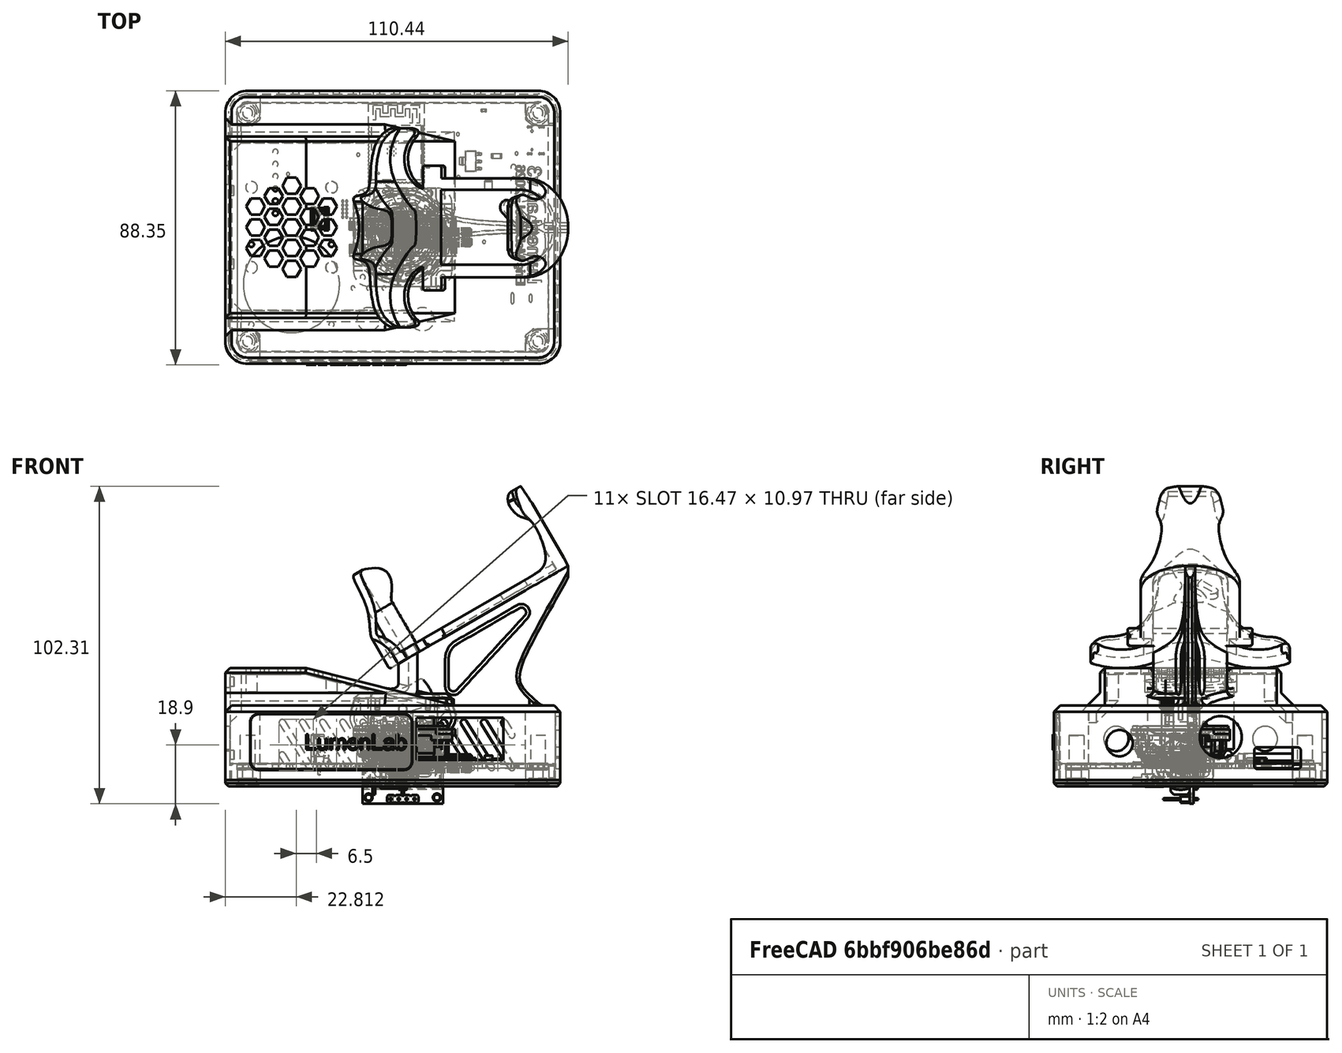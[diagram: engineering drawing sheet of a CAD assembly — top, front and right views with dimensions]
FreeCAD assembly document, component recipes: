
FREECAD ASSEMBLY — COMPONENT RECIPES ("lumenlab-platform-enclosure")

This assembly document has 22 components, labeled P0..P21 below (a component is one placed body or linked part). 21 of them carry a construction recipe — the FreeCAD feature program that regenerates the part from scratch, quoted from this document or its linked companion documents; the rest are supplied as boundary geometry only. No exploded tour is included for this assembly.
NOTE — this tour is split across 2 documents so each fits a 32k-token context. This is document 1: the component sections continue in the remaining 1 document, each repeating the header above.
COMPONENT P0 — geometry summary ("lumenlab-pcb001"; no construction recipe available for this part):
  bounding box: 106.5 x 80.0 x 42.6 mm
  tessellated surface: 375,475 triangles
  volume: 30416 mm^3 (8% of its bounding box)
COMPONENT P1 — recipe-attached ("lid", modeled in this document).
Construction recipe (the document's own serialized feature program — sketch geometry with constraints, then the solid features built on it; lengths are millimeters unless a unit is written):

FEATURE [PartDesign::SubShapeBinder] Binder
  BindCopyOnChange = 0
  BindMode = 0
  ClaimChildren = false
  Context = -> Body [Binder.]
  Fuse = false
  MakeFace = true
  OffsetFill = false
  OffsetIntersection = false
  OffsetJoinType = 0
  OffsetOpenResult = false
  PartialLoad = false
  Refine = true
  Relative = true
  Support = -> [Board_aaa008]
  _Version = 2
FEATURE [Sketcher::SketchObject] Sketch
  ArcFitTolerance = 1e-06
  AttachmentOffset = pos=(0,0,3.75) rot=(0,0,1;0rad)
  AttachmentSupport = -> [Binder]
  ExternalGeometry = -> [Binder]
  ExternalTypes = [0]
  FullyConstrained = true
  MakeInternals = false
  MapMode = 5
  Placement = pos=(0,0,-5.3502) rot=(1,0,0;3.14159rad)
  _ExternalGeoVersion = 0
  sketch-geometry (10):
    g0: LineSegment StartX=-57.1492 StartY=33.5464 StartZ=0 EndX=-57.1492 EndY=-39.9989 EndZ=0
    g1: LineSegment StartX=-49.9485 StartY=-47.1996 StartZ=0 EndX=43.5501 EndY=-47.1996 EndZ=0
    g2: LineSegment StartX=50.7508 StartY=-39.9989 StartZ=0 EndX=50.7508 EndY=33.5464 EndZ=0
    g3: LineSegment StartX=43.5501 StartY=40.7472 StartZ=0 EndX=-49.9485 EndY=40.7472 EndZ=0
    g4: ArcOfCircle CenterX=-49.9485 CenterY=33.5464 CenterZ=0 NormalX=0 NormalY=0 NormalZ=1 AngleXU=0 Radius=7.20071 StartAngle=1.5708 EndAngle=3.14159
    g5: ArcOfCircle CenterX=-49.9485 CenterY=-39.9989 CenterZ=0 NormalX=0 NormalY=0 NormalZ=1 AngleXU=0 Radius=7.20071 StartAngle=3.14159 EndAngle=4.71239
    g6: ArcOfCircle CenterX=43.5501 CenterY=-39.9989 CenterZ=0 NormalX=0 NormalY=0 NormalZ=1 AngleXU=0 Radius=7.20071 StartAngle=4.71239 EndAngle=6.28319
    g7: ArcOfCircle CenterX=43.5501 CenterY=33.5464 CenterZ=0 NormalX=0 NormalY=0 NormalZ=1 AngleXU=0 Radius=7.20071 StartAngle=1e-16 EndAngle=1.5708
    g8: GeomPoint [constr] X=-57.1492 Y=40.7472 Z=0
    g9: GeomPoint [constr] X=50.7508 Y=-47.1996 Z=0
  constraints (23):
    c: Tangent(g0,g4) = -1.5708
    c: Tangent(g0,g5) = -1.5708
    c: Tangent(g1,g5) = -1.5708
    c: Tangent(g1,g6) = -1.5708
    c: Tangent(g2,g6) = -1.5708
    c: Tangent(g2,g7) = -1.5708
    c: Tangent(g3,g7) = -1.5708
    c: Tangent(g3,g4) = -1.5708
    c: Vertical(g0)
    c: Vertical(g2)
    c: Horizontal(g1)
    c: Horizontal(g3)
    c: Equal(g4,g5)
    c: Equal(g5,g6)
    c: Equal(g6,g7)
    c: PointOnObject(g8,g0)
    c: PointOnObject(g8,g3)
    c: PointOnObject(g9,g1)
    c: PointOnObject(g9,g2)
    c: DistanceX(g0,g-5) = 4  'enclosure-width'
    c: Coincident(g4,g-4)
    c: Distance(g-7,g2) = 4
    c: Distance(g-9,g1) = 4
FEATURE [PartDesign::Pad] Pad
  Direction = (0,0,-1)
  Length = 2
  Length2 = 10
  Profile = -> Sketch
  ReferenceAxis = -> Sketch [N_Axis]
  Refine = true
  SideType = 0
  Suppressed = false
  Type = 0
  Type2 = 0
FEATURE [Sketcher::SketchObject] Sketch001
  ArcFitTolerance = 1e-06
  AttachmentSupport = -> [Pad]
  ExternalGeometry = -> [Binder]
  ExternalTypes = [0]
  FullyConstrained = true
  MakeInternals = false
  MapMode = 5
  Placement = pos=(0,0,-5.3502) rot=(0,0,1;0rad)
  _ExternalGeoVersion = 0
  sketch-geometry (20):
    g0: LineSegment StartX=-55.15 StartY=39.9996 StartZ=0 EndX=-55.15 EndY=-33.5498 EndZ=0
    g1: LineSegment StartX=-49.95 StartY=-38.7498 StartZ=0 EndX=43.551 EndY=-38.7498 EndZ=0
    g2: LineSegment StartX=48.751 StartY=-33.5498 StartZ=0 EndX=48.751 EndY=39.9996 EndZ=0
    g3: LineSegment StartX=43.551 StartY=45.1996 StartZ=0 EndX=-49.95 EndY=45.1996 EndZ=0
    g4: ArcOfCircle CenterX=-49.95 CenterY=39.9996 CenterZ=0 NormalX=0 NormalY=0 NormalZ=1 AngleXU=0 Radius=5.19999 StartAngle=1.5708 EndAngle=3.14159
    g5: ArcOfCircle CenterX=-49.95 CenterY=-33.5498 CenterZ=0 NormalX=0 NormalY=0 NormalZ=1 AngleXU=0 Radius=5.19999 StartAngle=3.14159 EndAngle=4.71239
    g6: ArcOfCircle CenterX=43.551 CenterY=-33.5498 CenterZ=0 NormalX=0 NormalY=0 NormalZ=1 AngleXU=0 Radius=5.19999 StartAngle=4.71239 EndAngle=6.28319
    g7: ArcOfCircle CenterX=43.551 CenterY=39.9996 CenterZ=0 NormalX=0 NormalY=0 NormalZ=1 AngleXU=0 Radius=5.19999 StartAngle=5e-16 EndAngle=1.5708
    g8: GeomPoint [constr] X=-55.15 Y=45.1996 Z=0
    g9: GeomPoint [constr] X=48.751 Y=-38.7498 Z=0
    g10: LineSegment StartX=-53.35 StartY=39.9996 StartZ=0 EndX=-53.35 EndY=-33.5498 EndZ=0
    g11: LineSegment StartX=-49.95 StartY=-36.9498 StartZ=0 EndX=43.551 EndY=-36.9498 EndZ=0
    g12: LineSegment StartX=46.951 StartY=-33.5498 StartZ=0 EndX=46.951 EndY=39.9996 EndZ=0
    g13: LineSegment StartX=43.551 StartY=43.3996 StartZ=0 EndX=-49.95 EndY=43.3996 EndZ=0
    g14: ArcOfCircle CenterX=-49.95 CenterY=39.9996 CenterZ=0 NormalX=0 NormalY=0 NormalZ=1 AngleXU=0 Radius=3.39999 StartAngle=1.5708 EndAngle=3.14159
    g15: ArcOfCircle CenterX=-49.95 CenterY=-33.5498 CenterZ=0 NormalX=0 NormalY=0 NormalZ=1 AngleXU=0 Radius=3.39999 StartAngle=3.14159 EndAngle=4.71239
    g16: ArcOfCircle CenterX=43.551 CenterY=-33.5498 CenterZ=0 NormalX=0 NormalY=0 NormalZ=1 AngleXU=0 Radius=3.39999 StartAngle=4.71239 EndAngle=6.28319
    g17: ArcOfCircle CenterX=43.551 CenterY=39.9996 CenterZ=0 NormalX=0 NormalY=0 NormalZ=1 AngleXU=0 Radius=3.39999 StartAngle=0 EndAngle=1.5708
    g18: GeomPoint [constr] X=-53.35 Y=43.3996 Z=0
    g19: GeomPoint [constr] X=46.951 Y=-36.9498 Z=0
  constraints (46):
    c: Tangent(g0,g4) = -1.5708
    c: Tangent(g0,g5) = -1.5708
    c: Tangent(g1,g5) = -1.5708
    c: Tangent(g1,g6) = -1.5708
    c: Tangent(g2,g6) = -1.5708
    c: Tangent(g2,g7) = -1.5708
    c: Tangent(g3,g7) = -1.5708
    c: Tangent(g3,g4) = -1.5708
    c: Vertical(g0)
    c: Vertical(g2)
    c: Horizontal(g1)
    c: Horizontal(g3)
    c: Equal(g4,g5)
    c: Equal(g5,g6)
    c: Equal(g6,g7)
    c: PointOnObject(g8,g0)
    c: PointOnObject(g8,g3)
    c: PointOnObject(g9,g1)
    c: PointOnObject(g9,g2)
    c: DistanceX(g0,g-5) = 2
    c: Coincident(g4,g-4)
    c: DistanceX(g-7,g2) = 2
    c: DistanceY(g1,g-9) = 2
    c: Tangent(g10,g14) = -1.5708
    c: Tangent(g10,g15) = -1.5708
    c: Tangent(g11,g15) = -1.5708
    c: Tangent(g11,g16) = -1.5708
    c: Tangent(g12,g16) = -1.5708
    c: Tangent(g12,g17) = -1.5708
    c: Tangent(g13,g17) = -1.5708
    c: Tangent(g13,g14) = -1.5708
    c: Vertical(g10)
    c: Vertical(g12)
    c: Horizontal(g11)
    c: Horizontal(g13)
    c: Equal(g14,g15)
    c: Equal(g15,g16)
    c: Equal(g16,g17)
    c: PointOnObject(g18,g10)
    c: PointOnObject(g18,g13)
    c: PointOnObject(g19,g11)
    c: PointOnObject(g19,g12)
    c: DistanceX(g10,g-5) = 0.2
    c: DistanceX(g-7,g12) = 0.2
    c: DistanceY(g11,g-9) = 0.2
    c: Coincident(g14,g4)
FEATURE [PartDesign::Pad] Pad001
  BaseFeature = -> Pad
  Direction = (0,0,1)
  Length = 5
  Length2 = 10
  Profile = -> Sketch001
  ReferenceAxis = -> Sketch001 [N_Axis]
  Refine = true
  SideType = 0
  Suppressed = false
  Type = 0
  Type2 = 0
FEATURE [Sketcher::SketchObject] Sketch002
  ArcFitTolerance = 1e-06
  ExternalGeometry = -> [Binder,Pad001]
  ExternalTypes = [0]
  FullyConstrained = true
  MakeInternals = false
  MapMode = 5
  Placement = pos=(0,0,-2) rot=(1,0,0;3.14159rad)
  _ExternalGeoVersion = 0
  sketch-geometry (10):
    g0: LineSegment StartX=-53.1492 StartY=29.5498 StartZ=0 EndX=-53.35 EndY=29.5498 EndZ=0
    g1: LineSegment StartX=-45.95 StartY=36.7473 StartZ=0 EndX=-45.95 EndY=36.9498 EndZ=0
    g2: LineSegment StartX=-45.95 StartY=36.9498 StartZ=0 EndX=-49.95 EndY=36.9498 EndZ=0
    g3: LineSegment StartX=-53.35 StartY=29.5498 StartZ=0 EndX=-53.35 EndY=33.5498 EndZ=0
    g4: ArcOfCircle CenterX=-49.95 CenterY=33.5498 CenterZ=0 NormalX=0 NormalY=0 NormalZ=1 AngleXU=0 Radius=3.39999 StartAngle=1.5708 EndAngle=3.14159
    g5: LineSegment StartX=-53.1492 StartY=29.5498 StartZ=0 EndX=-48.6466 EndY=29.5498 EndZ=0
    g6: ArcOfCircle CenterX=-48.6466 CenterY=30.4451 CenterZ=0 NormalX=0 NormalY=0 NormalZ=1 AngleXU=0 Radius=0.895293 StartAngle=4.71239 EndAngle=5.38086
    g7: LineSegment StartX=-48.0918 StartY=29.7425 StartZ=0 EndX=-46.138 EndY=31.2855 EndZ=0
    g8: ArcOfCircle CenterX=-46.4444 CenterY=31.6735 CenterZ=0 NormalX=0 NormalY=0 NormalZ=1 AngleXU=0 Radius=0.494368 StartAngle=5.38086 EndAngle=6.28319
    g9: LineSegment StartX=-45.95 StartY=31.6735 StartZ=0 EndX=-45.95 EndY=36.7473 EndZ=0
  constraints (24):
    c: PointOnObject(g0,g-8)
    c: Horizontal(g0)
    c: PointOnObject(g1,g-7)
    c: Vertical(g1)
    c: Coincident(g2,g1)
    c: Coincident(g2,g-9)
    c: Coincident(g3,g0)
    c: Coincident(g3,g-9)
    c: Coincident(g4,g2)
    c: Coincident(g4,g3)
    c: PointOnObject(g0,g-10)
    c: PointOnObject(g1,g-11)
    c: DistanceY(g3,g3) = 4
    c: DistanceX(g2,g2) = 4
    c: Equal(g4,g-9)
    c: Coincident(g0,g5)
    c: Tangent(g5,g6) = -1.5708
    c: Tangent(g6,g7) = -1.5708
    c: Tangent(g7,g8) = -1.5708
    c: Tangent(g8,g9) = -1.5708
    c: Vertical(g9)
    c: Coincident(g9,g1)
    c: Horizontal(g5)
    c: Block(g7)
FEATURE [PartDesign::Pad] Pad002
  BaseFeature = -> Pad001
  Direction = (0,-1e-16,-1)
  Length = 10
  Length2 = 10
  Profile = -> Sketch002
  ReferenceAxis = -> Sketch002 [N_Axis]
  Refine = true
  SideType = 0
  Suppressed = false
  Type = 2
  Type2 = 0
FEATURE [PartDesign::Plane] DatumPlane
  AttachmentOffset = pos=(0,0,0) rot=(1,0,0;1.5708rad)
  AttachmentSupport = -> [Pad002]
  Length = 122.59
  MapMode = 45
  Placement = pos=(-3.1995,3.22491,-2.8502) rot=(1,0,0;1.5708rad)
  ResizeMode = 0
  Width = 64.6901
  expr: .AttachmentOffset.Rotation.Pitch = 0
FEATURE [PartDesign::Plane] DatumPlane001
  AttachmentOffset = pos=(0,0,0) rot=(1,0,0;1.5708rad)
  AttachmentSupport = -> [Pad002]
  Length = 101.209
  MapMode = 45
  Placement = pos=(-3.1995,3.22491,-2.8502) rot=(0.57735,0.57735,0.57735;2.0944rad)
  ResizeMode = 0
  Width = 63.2625
FEATURE [PartDesign::Line] DatumLine
  AttacherType = Attacher::AttachEngineLine
  AttachmentSupport = -> [DatumPlane001,DatumPlane]
  Length = 20
  MapMode = 30
  Placement = pos=(-3.1995,3.22491,-2.8502) rot=(0,1,0;3.14159rad)
  ResizeMode = 0
FEATURE [PartDesign::Mirrored] Mirrored
  BaseFeature = -> Pad002
  MirrorPlane = -> DatumPlane
  Originals = -> [Pad002]
  Refine = true
  Suppressed = false
  TransformMode = 0
FEATURE [PartDesign::Mirrored] Mirrored001
  BaseFeature = -> Mirrored
  MirrorPlane = -> DatumPlane001
  Originals = -> [Pad002]
  Refine = true
  Suppressed = false
  TransformMode = 0
FEATURE [PartDesign::PolarPattern] PolarPattern
  Angle = 360
  Axis = -> DatumLine
  BaseFeature = -> Mirrored001
  Mode = 0
  Occurrences = 2
  Offset = 120
  Originals = -> [Pad002]
  Refine = true
  Reversed = true
  SpacingPattern = [0]
  Spacings = [-1]
  Suppressed = false
  TransformMode = 0
FEATURE [Sketcher::SketchObject] Sketch003
  ArcFitTolerance = 1e-06
  AttachmentSupport = -> [PolarPattern]
  ExternalTypes = [0]
  FullyConstrained = true
  MakeInternals = false
  MapMode = 5
  Placement = pos=(0,0,-2) rot=(0,0,1;0rad)
  _ExternalGeoVersion = 0
  sketch-geometry (1):
    g0: Circle CenterX=-49.95 CenterY=-33.5498 CenterZ=0 NormalX=0 NormalY=0 NormalZ=1 AngleXU=0 Radius=1.625
  constraints (2):
    c: Coincident(g0,g-3)
    c: Diameter(g0) = 3.25
FEATURE [PartDesign::Pocket] Pocket
  BaseFeature = -> PolarPattern
  Direction = (0,0,-1)
  Length = 4.35
  Length2 = 5
  Profile = -> Sketch003
  ReferenceAxis = -> Sketch003 [N_Axis]
  Refine = true
  SideType = 0
  Suppressed = false
  Type = 1
  Type2 = 0
FEATURE [PartDesign::Mirrored] Mirrored002
  BaseFeature = -> Pocket
  MirrorPlane = -> DatumPlane
  Originals = -> [Pocket]
  Refine = true
  Suppressed = false
  TransformMode = 0
FEATURE [PartDesign::Mirrored] Mirrored003
  BaseFeature = -> Mirrored002
  MirrorPlane = -> DatumPlane001
  Originals = -> [Pocket]
  Refine = true
  Suppressed = false
  TransformMode = 0
FEATURE [PartDesign::PolarPattern] PolarPattern001
  Angle = 360
  Axis = -> DatumLine
  BaseFeature = -> Mirrored003
  Mode = 0
  Occurrences = 2
  Offset = 120
  Originals = -> [Pocket]
  Refine = true
  SpacingPattern = [0]
  Spacings = [-1]
  Suppressed = false
  TransformMode = 0
FEATURE [Sketcher::SketchObject] Sketch046
  ArcFitTolerance = 1e-06
  AttachmentSupport = -> [PolarPattern001]
  ExternalGeometry = -> [PolarPattern001]
  ExternalTypes = [0,0,0,0]
  FullyConstrained = true
  MakeInternals = false
  MapMode = 5
  Placement = pos=(0,0,-7.3502) rot=(1,0,0;3.14159rad)
  _ExternalGeoVersion = 1
  sketch-geometry (4):
    g0: Circle CenterX=-49.95 CenterY=33.5498 CenterZ=0 NormalX=0 NormalY=0 NormalZ=1 AngleXU=0 Radius=3
    g1: Circle CenterX=43.551 CenterY=33.5498 CenterZ=0 NormalX=0 NormalY=0 NormalZ=1 AngleXU=0 Radius=3
    g2: Circle CenterX=43.551 CenterY=-39.9996 CenterZ=0 NormalX=0 NormalY=0 NormalZ=1 AngleXU=0 Radius=3
    g3: Circle CenterX=-49.95 CenterY=-39.9996 CenterZ=0 NormalX=0 NormalY=0 NormalZ=1 AngleXU=0 Radius=3
  constraints (8):
    c: Coincident(g0,g-6)
    c: Coincident(g1,g-5)
    c: Coincident(g2,g-4)
    c: Coincident(g3,g-3)
    c: Diameter(g0) = 6
    c: Equal(g0,g1)
    c: Equal(g0,g3)
    c: Equal(g0,g2)
FEATURE [PartDesign::Pocket] Pocket023
  BaseFeature = -> PolarPattern001
  Direction = (0,0,1)
  Length = 2.5
  Length2 = 5
  Profile = -> Sketch046
  ReferenceAxis = -> Sketch046 [N_Axis]
  Refine = true
  SideType = 0
  Suppressed = false
  Type = 0
  Type2 = 0
FEATURE [Sketcher::SketchObject] Sketch067
  ArcFitTolerance = 1e-06
  AttachmentSupport = -> [Pocket023]
  ExternalGeometry = -> [Pocket023]
  ExternalTypes = [0,0,0,0]
  FullyConstrained = true
  MakeInternals = false
  MapMode = 5
  Placement = pos=(0,0,-7.3502) rot=(1,0,0;3.14159rad)
  _ExternalGeoVersion = 1
  sketch-geometry (4):
    g0: Circle CenterX=-49.95 CenterY=33.5498 CenterZ=0 NormalX=0 NormalY=0 NormalZ=1 AngleXU=0 Radius=3.625
    g1: Circle CenterX=43.551 CenterY=33.5498 CenterZ=0 NormalX=0 NormalY=0 NormalZ=1 AngleXU=0 Radius=3.625
    g2: Circle CenterX=43.551 CenterY=-39.9996 CenterZ=0 NormalX=0 NormalY=0 NormalZ=1 AngleXU=0 Radius=3.625
    g3: Circle CenterX=-49.95 CenterY=-39.9996 CenterZ=0 NormalX=0 NormalY=0 NormalZ=1 AngleXU=0 Radius=3.625
  constraints (8):
    c: Diameter(g0) = 7.25
    c: Coincident(g0,g-3)
    c: Coincident(g1,g-4)
    c: Coincident(g2,g-5)
    c: Coincident(g3,g-6)
    c: Equal(g0,g1)
    c: Equal(g0,g3)
    c: Equal(g0,g2)
FEATURE [PartDesign::Pocket] Pocket033
  BaseFeature = -> Pocket023
  Direction = (0,0,1)
  Length = 0.5
  Length2 = 5
  Profile = -> Sketch067
  ReferenceAxis = -> Sketch067 [N_Axis]
  Refine = true
  SideType = 0
  Suppressed = false
  Type = 0
  Type2 = 0
FEATURE [Part::Part2DObjectPython] ShapeString002  # Draft 2D object (typed FeaturePython)
  FontFile = <path>
  Fuse = false
  Justification = 6
  JustificationReference = 0
  KeepLeftMargin = false
  MakeFace = true
  ObliqueAngle = 0
  Placement = pos=(40.1807,-14.5677,-7.3502) rot=(0.707107,0.707107,0;3.14159rad)
  ScaleToSize = true
  Size = 4.5
  String = LumenLab v3
  Tracking = 0
FEATURE [Part::Part2DObjectPython] ShapeString003  # Draft 2D object (typed FeaturePython)
  FontFile = <path>
  Fuse = false
  Justification = 6
  JustificationReference = 0
  KeepLeftMargin = false
  MakeFace = true
  ObliqueAngle = 0
  Placement = pos=(36.4305,-15.2766,-7.3502) rot=(0.707107,0.707107,0;3.14159rad)
  ScaleToSize = true
  Size = 3
  String = Eric McDaniel - 2026
  Tracking = 0
FEATURE [PartDesign::Chamfer] Chamfer014
  Angle = 45
  Base = -> Pocket033 [Edge24]
  BaseFeature = -> Pocket033
  ChamferType = 0
  FlipDirection = false
  Refine = true
  Size = 1
  Size2 = 1
  SupportTransform = false
  Suppressed = false
  UseAllEdges = false
FEATURE [PartDesign::Pocket] Pocket034
  BaseFeature = -> Chamfer014
  Direction = (0,0,1)
  Length = 0.5
  Length2 = 5
  Profile = -> ShapeString002
  ReferenceAxis = -> ShapeString002 [N_Axis]
  Refine = true
  SideType = 0
  Suppressed = false
  Type = 0
  Type2 = 0
FEATURE [PartDesign::Pocket] Pocket035
  BaseFeature = -> Pocket034
  Direction = (0,0,1)
  Length = 0.5
  Length2 = 5
  Profile = -> ShapeString003
  ReferenceAxis = -> ShapeString003 [N_Axis]
  Refine = true
  SideType = 0
  Suppressed = false
  Type = 0
  Type2 = 0
FEATURE [Sketcher::SketchObject] Sketch070
  ArcFitTolerance = 1e-06
  AttachmentSupport = -> [Pocket035]
  ExternalGeometry = -> [Pocket035]
  ExternalTypes = [0,0,0,0]
  FullyConstrained = true
  MakeInternals = false
  MapMode = 5
  Placement = pos=(48.751,0,0) rot=(0.57735,0.57735,0.57735;2.0944rad)
  _ExternalGeoVersion = 1
  sketch-geometry (4):
    g0: LineSegment StartX=35.9996 StartY=-5.3502 StartZ=0 EndX=35.9996 EndY=-0.350198 EndZ=0
    g1: LineSegment StartX=35.9996 StartY=-0.350198 StartZ=0 EndX=2.99961 EndY=-0.350198 EndZ=0
    g2: LineSegment StartX=2.99961 StartY=-0.350198 StartZ=0 EndX=2.99961 EndY=-5.3502 EndZ=0
    g3: LineSegment StartX=2.99961 StartY=-5.3502 StartZ=0 EndX=35.9996 EndY=-5.3502 EndZ=0
  constraints (12):
    c: Coincident(g0,g1)
    c: Coincident(g2,g3)
    c: Coincident(g3,g0)
    c: Vertical(g0)
    c: Vertical(g2)
    c: Horizontal(g1)
    c: Horizontal(g3)
    c: PointOnObject(g0,g-4)
    c: PointOnObject(g-3,g0)
    c: Coincident(g2,g1)
    c: PointOnObject(g1,g-5)
    c: DistanceX(g1,g1) = 33
FEATURE [PartDesign::Pocket] Pocket037
  BaseFeature = -> Pocket035
  Direction = (-1,0,0)
  Length = 5
  Length2 = 5
  Profile = -> Sketch070
  ReferenceAxis = -> Sketch070 [N_Axis]
  Refine = true
  SideType = 0
  Suppressed = false
  Type = 2
  Type2 = 0
FEATURE [PartDesign::Chamfer] Chamfer015
  Angle = 45
  Base = -> Pocket037 [Edge1565,Edge1564,Edge1554]
  BaseFeature = -> Pocket037
  ChamferType = 0
  FlipDirection = false
  Refine = true
  Size = 0.6
  Size2 = 1
  SupportTransform = false
  Suppressed = false
  UseAllEdges = false
FEATURE [PartDesign::Body] Body  label="lid"
  AllowCompound = false
  Group = -> [Binder,Sketch,Pad,Sketch001,Pad001,Sketch002,Pad002,DatumPlane,Mirrored,DatumPlane001,Mirrored001,DatumLine,PolarPattern,Sketch003,Pocket,Mirrored002,Mirrored003,PolarPattern001,Sketch046,Pocket023,Sketch067,Pocket033,Chamfer014,ShapeString002,ShapeString003,Pocket034,Pocket035,Sketch070,Pocket037,Chamfer015]
  Origin = -> Origin032
  Tip = -> Chamfer015
COMPONENT P2 — recipe-attached ("body", modeled in this document).
Construction recipe (the document's own serialized feature program — sketch geometry with constraints, then the solid features built on it; lengths are millimeters unless a unit is written):

FEATURE [PartDesign::SubShapeBinder] Binder001
  BindCopyOnChange = 0
  BindMode = 0
  ClaimChildren = false
  Context = -> Body001 [Binder001.]
  Fuse = false
  MakeFace = true
  OffsetFill = false
  OffsetIntersection = false
  OffsetJoinType = 0
  OffsetOpenResult = false
  PartialLoad = false
  Refine = true
  Relative = true
  Support = -> [Board_aaa008]
  _Version = 2
FEATURE [Sketcher::SketchObject] Sketch010
  ArcFitTolerance = 1e-06
  AttachmentOffset = pos=(0,0,3.75) rot=(0,0,1;0rad)
  AttachmentSupport = -> [Binder001]
  ExternalGeometry = -> [Binder001]
  ExternalTypes = [0]
  FullyConstrained = true
  MakeInternals = false
  MapMode = 5
  Placement = pos=(0,0,-5.3502) rot=(1,0,0;3.14159rad)
  _ExternalGeoVersion = 0
  sketch-geometry (19):
    g0: LineSegment StartX=-57.1492 StartY=33.5464 StartZ=0 EndX=-57.1492 EndY=-39.9996 EndZ=0
    g1: LineSegment StartX=-49.9492 StartY=-47.1996 StartZ=0 EndX=43.5508 EndY=-47.1996 EndZ=0
    g2: LineSegment StartX=50.7508 StartY=-39.9996 StartZ=0 EndX=50.7508 EndY=33.5464 EndZ=0
    g3: LineSegment StartX=43.5508 StartY=40.7464 StartZ=0 EndX=-49.9492 EndY=40.7464 EndZ=0
    g4: ArcOfCircle CenterX=-49.9492 CenterY=33.5464 CenterZ=0 NormalX=0 NormalY=0 NormalZ=1 AngleXU=0 Radius=7.19996 StartAngle=1.5708 EndAngle=3.14159
    g5: ArcOfCircle CenterX=-49.9492 CenterY=-39.9996 CenterZ=0 NormalX=0 NormalY=0 NormalZ=1 AngleXU=0 Radius=7.19996 StartAngle=3.14159 EndAngle=4.71239
    g6: ArcOfCircle CenterX=43.5508 CenterY=-39.9996 CenterZ=0 NormalX=0 NormalY=0 NormalZ=1 AngleXU=0 Radius=7.19996 StartAngle=4.71239 EndAngle=6.28319
    g7: ArcOfCircle CenterX=43.5508 CenterY=33.5464 CenterZ=0 NormalX=0 NormalY=0 NormalZ=1 AngleXU=0 Radius=7.19996 StartAngle=0 EndAngle=1.5708
    g8: GeomPoint [constr] X=-57.1492 Y=40.7464 Z=0
    g9: GeomPoint [constr] X=50.7508 Y=-47.1996 Z=0
    g10: LineSegment StartX=-49.9492 StartY=-45.5996 StartZ=0 EndX=43.5508 EndY=-45.5996 EndZ=0
    g11: LineSegment StartX=49.1508 StartY=-39.9996 StartZ=0 EndX=49.1508 EndY=33.5464 EndZ=0
    g12: LineSegment StartX=43.5508 StartY=39.1464 StartZ=0 EndX=-49.9492 EndY=39.1464 EndZ=0
    g13: LineSegment StartX=-55.5492 StartY=33.5464 StartZ=0 EndX=-55.5492 EndY=-39.9996 EndZ=0
    g14: ArcOfCircle CenterX=-49.9492 CenterY=-39.9996 CenterZ=0 NormalX=0 NormalY=0 NormalZ=1 AngleXU=0 Radius=5.59996 StartAngle=3.14159 EndAngle=4.71239
    g15: ArcOfCircle CenterX=43.5508 CenterY=-39.9996 CenterZ=0 NormalX=0 NormalY=0 NormalZ=1 AngleXU=0 Radius=5.59996 StartAngle=4.71239 EndAngle=6.28319
    g16: ArcOfCircle CenterX=43.5508 CenterY=33.5464 CenterZ=0 NormalX=0 NormalY=0 NormalZ=1 AngleXU=0 Radius=5.59996 StartAngle=4e-16 EndAngle=1.5708
    g17: ArcOfCircle CenterX=-49.9492 CenterY=33.5464 CenterZ=0 NormalX=0 NormalY=0 NormalZ=1 AngleXU=0 Radius=5.59996 StartAngle=1.5708 EndAngle=3.14159
    g18: GeomPoint [constr] X=-55.5492 Y=-45.5996 Z=0
  constraints (43):
    c: Tangent(g0,g4) = -1.5708
    c: Tangent(g0,g5) = -1.5708
    c: Tangent(g1,g5) = -1.5708
    c: Tangent(g1,g6) = -1.5708
    c: Tangent(g2,g6) = -1.5708
    c: Tangent(g2,g7) = -1.5708
    c: Tangent(g3,g7) = -1.5708
    c: Tangent(g3,g4) = -1.5708
    c: Vertical(g0)
    c: Vertical(g2)
    c: Horizontal(g1)
    c: Horizontal(g3)
    c: Equal(g4,g5)
    c: Equal(g5,g6)
    c: Equal(g6,g7)
    c: PointOnObject(g8,g0)
    c: PointOnObject(g8,g3)
    c: PointOnObject(g9,g1)
    c: PointOnObject(g9,g2)
    c: Distance(g0,g-3) = 4
    c: Coincident(g-10,g4)
    c: Distance(g2,g-7) = 4
    c: Distance(g1,g-4) = 4
    c: Tangent(g10,g14) = -1.5708
    c: Tangent(g10,g15) = -1.5708
    c: Tangent(g11,g15) = -1.5708
    c: Tangent(g11,g16) = -1.5708
    c: Tangent(g12,g16) = -1.5708
    c: Tangent(g12,g17) = -1.5708
    c: Tangent(g13,g17) = -1.5708
    c: Tangent(g13,g14) = -1.5708
    c: Horizontal(g10)
    c: Horizontal(g12)
    c: Vertical(g11)
    c: Vertical(g13)
    c: Equal(g14,g15)
    c: Equal(g15,g16)
    c: Equal(g16,g17)
    c: PointOnObject(g18,g10)
    c: PointOnObject(g18,g13)
    c: Distance(g0,g13) = 1.6
    c: Coincident(g14,g5)
    c: Coincident(g16,g7)
FEATURE [PartDesign::Pad] Pad003
  Direction = (0,0,-1)
  Length = 22
  Length2 = 10
  Profile = -> Sketch010
  ReferenceAxis = -> Sketch010 [N_Axis]
  Refine = true
  Reversed = true
  SideType = 0
  Suppressed = false
  Type = 0
  Type2 = 0
FEATURE [Sketcher::SketchObject] Sketch011
  ArcFitTolerance = 1e-06
  AttachmentSupport = -> [Pad003]
  ExternalGeometry = -> [Pad003]
  ExternalTypes = [0]
  FullyConstrained = true
  MakeInternals = false
  MapMode = 5
  Placement = pos=(0,0,16.6498) rot=(0,0,1;0rad)
  _ExternalGeoVersion = 0
  sketch-geometry (10):
    g0: LineSegment StartX=-57.1492 StartY=39.9996 StartZ=0 EndX=-57.1492 EndY=-33.5464 EndZ=0
    g1: LineSegment StartX=-49.9492 StartY=-40.7464 StartZ=0 EndX=43.5508 EndY=-40.7464 EndZ=0
    g2: LineSegment StartX=50.7508 StartY=-33.5464 StartZ=0 EndX=50.7508 EndY=39.9996 EndZ=0
    g3: LineSegment StartX=43.5508 StartY=47.1996 StartZ=0 EndX=-49.9492 EndY=47.1996 EndZ=0
    g4: ArcOfCircle CenterX=-49.9492 CenterY=39.9996 CenterZ=0 NormalX=0 NormalY=0 NormalZ=1 AngleXU=0 Radius=7.19996 StartAngle=1.5708 EndAngle=3.14159
    g5: ArcOfCircle CenterX=-49.9492 CenterY=-33.5464 CenterZ=0 NormalX=0 NormalY=0 NormalZ=1 AngleXU=0 Radius=7.19996 StartAngle=3.14159 EndAngle=4.71239
    g6: ArcOfCircle CenterX=43.5508 CenterY=-33.5464 CenterZ=0 NormalX=0 NormalY=0 NormalZ=1 AngleXU=0 Radius=7.19996 StartAngle=4.71239 EndAngle=6.28319
    g7: ArcOfCircle CenterX=43.5508 CenterY=39.9996 CenterZ=0 NormalX=0 NormalY=0 NormalZ=1 AngleXU=0 Radius=7.19996 StartAngle=0 EndAngle=1.5708
    g8: GeomPoint [constr] X=-57.1492 Y=47.1996 Z=0
    g9: GeomPoint [constr] X=50.7508 Y=-40.7464 Z=0
  constraints (20):
    c: Tangent(g0,g4) = -1.5708
    c: Tangent(g0,g5) = -1.5708
    c: Tangent(g1,g5) = -1.5708
    c: Tangent(g1,g6) = -1.5708
    c: Tangent(g2,g6) = -1.5708
    c: Tangent(g2,g7) = -1.5708
    c: Tangent(g3,g7) = -1.5708
    c: Tangent(g3,g4) = -1.5708
    c: Vertical(g2)
    c: Horizontal(g1)
    c: Equal(g4,g5)
    c: Equal(g5,g6)
    c: PointOnObject(g8,g0)
    c: PointOnObject(g8,g3)
    c: PointOnObject(g9,g1)
    c: PointOnObject(g9,g2)
    c: Coincident(g-5,g0)
    c: Coincident(g3,g-4)
    c: Coincident(g3,g-6)
    c: Coincident(g1,g-9)
FEATURE [PartDesign::Pad] Pad004
  BaseFeature = -> Pad003
  Direction = (0,0,1)
  Length = 2
  Length2 = 10
  Profile = -> Sketch011
  ReferenceAxis = -> Sketch011 [N_Axis]
  Refine = true
  SideType = 0
  Suppressed = false
  Type = 0
  Type2 = 0
FEATURE [Sketcher::SketchObject] Sketch013
  ArcFitTolerance = 1e-06
  ExternalGeometry = -> [Binder001]
  ExternalTypes = [0]
  FullyConstrained = true
  MakeInternals = false
  MapMode = 5
  Placement = pos=(50.7508,0,3.061e-13) rot=(0.57735,0.57735,0.57735;2.0944rad)
  _ExternalGeoVersion = 0
  sketch-geometry (13):
    g0: LineSegment StartX=23.7009 StartY=4.155 StartZ=0 EndX=23.7009 EndY=-0.845 EndZ=0
    g1: LineSegment StartX=24.7009 StartY=-1.845 StartZ=0 EndX=37.7009 EndY=-1.845 EndZ=0
    g2: LineSegment StartX=38.7009 StartY=-0.845 StartZ=0 EndX=38.7009 EndY=4.155 EndZ=0
    g3: LineSegment StartX=37.7009 StartY=5.155 StartZ=0 EndX=24.7009 EndY=5.155 EndZ=0
    g4: ArcOfCircle CenterX=24.7009 CenterY=4.155 CenterZ=0 NormalX=0 NormalY=0 NormalZ=1 AngleXU=0 Radius=1 StartAngle=1.5708 EndAngle=3.14159
    g5: ArcOfCircle CenterX=24.7009 CenterY=-0.845 CenterZ=0 NormalX=0 NormalY=0 NormalZ=1 AngleXU=0 Radius=1 StartAngle=3.14159 EndAngle=4.71239
    g6: ArcOfCircle CenterX=37.7009 CenterY=-0.845 CenterZ=0 NormalX=0 NormalY=0 NormalZ=1 AngleXU=0 Radius=1 StartAngle=4.71239 EndAngle=6.28319
    g7: ArcOfCircle CenterX=37.7009 CenterY=4.155 CenterZ=0 NormalX=0 NormalY=0 NormalZ=1 AngleXU=0 Radius=1 StartAngle=2e-16 EndAngle=1.5708
    g8: GeomPoint [constr] X=23.7009 Y=5.155 Z=0
    g9: GeomPoint [constr] X=38.7009 Y=-1.845 Z=0
    g10: LineSegment [constr] StartX=28.0309 StartY=2.01 StartZ=0 EndX=24.7009 EndY=4.155 EndZ=0
    g11: LineSegment [constr] StartX=34.3709 StartY=2.01 StartZ=0 EndX=37.7009 EndY=4.155 EndZ=0
    g12: LineSegment [constr] StartX=28.0309 StartY=1.3 StartZ=0 EndX=24.7009 EndY=-0.845 EndZ=0
  constraints (30):
    c: Tangent(g0,g4) = -1.5708
    c: Tangent(g0,g5) = -1.5708
    c: Tangent(g1,g5) = -1.5708
    c: Tangent(g1,g6) = -1.5708
    c: Tangent(g2,g6) = -1.5708
    c: Tangent(g2,g7) = -1.5708
    c: Tangent(g3,g7) = -1.5708
    c: Tangent(g3,g4) = -1.5708
    c: Vertical(g0)
    c: Vertical(g2)
    c: Horizontal(g1)
    c: Horizontal(g3)
    c: Equal(g4,g5)
    c: Equal(g5,g6)
    c: Equal(g6,g7)
    c: PointOnObject(g8,g0)
    c: PointOnObject(g8,g3)
    c: PointOnObject(g9,g1)
    c: PointOnObject(g9,g2)
    c: Distance(g0,g2) = 15
    c: Distance(g1,g3) = 7
    c: Radius(g5) = 1
    c: Coincident(g10,g-6)
    c: Coincident(g10,g4)
    c: Coincident(g11,g-8)
    c: Coincident(g11,g7)
    c: Coincident(g12,g-3)
    c: Coincident(g12,g5)
    c: Equal(g10,g11)
    c: Equal(g10,g12)
FEATURE [PartDesign::Pocket] Pocket008
  BaseFeature = -> Pad004
  Direction = (-1,-1e-16,-5.9e-15)
  Length = 5
  Length2 = 5
  Profile = -> Sketch013
  ReferenceAxis = -> Sketch013 [N_Axis]
  Refine = true
  SideType = 0
  Suppressed = false
  Type = 2
  Type2 = 0
FEATURE [Sketcher::SketchObject] Sketch014
  ArcFitTolerance = 1e-06
  ExternalGeometry = -> [Binder001]
  ExternalTypes = [0,0]
  FullyConstrained = false
  MakeInternals = false
  MapMode = 5
  Placement = pos=(50.7508,0,2.944e-13) rot=(0.57735,0.57735,0.57735;2.0944rad)
  _ExternalGeoVersion = 0
  sketch-geometry (2):
    g0: Circle CenterX=-19.6504 CenterY=6.5 CenterZ=0 NormalX=0 NormalY=0 NormalZ=1 AngleXU=0 Radius=4.25
    g1: Circle CenterX=12.9172 CenterY=8.44815 CenterZ=0 NormalX=0 NormalY=0 NormalZ=1 AngleXU=0 Radius=6.75
  constraints (3):
    c: Coincident(g0,g-3)
    c: Diameter(g0) = 8.5
    c: Diameter(g1) = 13.5
FEATURE [PartDesign::Pocket] Pocket009
  BaseFeature = -> Pocket008
  Direction = (-1,0,-5.8e-15)
  Length = 5
  Length2 = 5
  Profile = -> Sketch014
  ReferenceAxis = -> Sketch014 [N_Axis]
  Refine = true
  SideType = 0
  Suppressed = false
  Type = 2
  Type2 = 0
FEATURE [Sketcher::SketchObject] Sketch015
  ArcFitTolerance = 1e-06
  ExternalGeometry = -> [Binder001]
  ExternalTypes = [0]
  FullyConstrained = true
  MakeInternals = false
  MapMode = 5
  Placement = pos=(0,0,0) rot=(1,0,0;3.14159rad)
  _ExternalGeoVersion = 0
  sketch-geometry (26):
    g0: LineSegment StartX=-55.5492 StartY=29.5464 StartZ=0 EndX=-49.9492 EndY=29.5464 EndZ=0
    g1: ArcOfCircle CenterX=-49.9492 CenterY=33.5464 CenterZ=0 NormalX=0 NormalY=0 NormalZ=1 AngleXU=0 Radius=4 StartAngle=4.71239 EndAngle=6.28319
    g2: LineSegment StartX=-45.9492 StartY=33.5464 StartZ=0 EndX=-45.9492 EndY=39.1464 EndZ=0
    g3: LineSegment StartX=-45.9492 StartY=39.1464 StartZ=0 EndX=-49.9492 EndY=39.1464 EndZ=0
    g4: ArcOfCircle CenterX=-49.9492 CenterY=33.5464 CenterZ=0 NormalX=0 NormalY=0 NormalZ=1 AngleXU=0 Radius=5.59996 StartAngle=1.5708 EndAngle=3.14159
    g5: LineSegment StartX=-55.5492 StartY=33.5464 StartZ=0 EndX=-55.5492 EndY=29.5464 EndZ=0
    g6: LineSegment StartX=-49.9492 StartY=-35.9996 StartZ=0 EndX=-55.5492 EndY=-35.9996 EndZ=0
    g7: LineSegment [constr] StartX=-55.5492 StartY=-39.9996 StartZ=0 EndX=-55.5492 EndY=-4.52586 EndZ=0
    g8: LineSegment StartX=-55.5492 StartY=-35.9996 StartZ=0 EndX=-55.5492 EndY=-39.9996 EndZ=0
    g9: ArcOfCircle CenterX=-49.9492 CenterY=-39.9996 CenterZ=0 NormalX=0 NormalY=0 NormalZ=1 AngleXU=0 Radius=5.59996 StartAngle=3.14159 EndAngle=4.71239
    g10: LineSegment StartX=-49.9492 StartY=-45.5996 StartZ=0 EndX=-45.9492 EndY=-45.5996 EndZ=0
    g11: LineSegment [constr] StartX=49.1508 StartY=-39.9996 StartZ=0 EndX=49.1508 EndY=-8.19439 EndZ=0
    g12: LineSegment StartX=43.5508 StartY=-45.5996 StartZ=0 EndX=39.5508 EndY=-45.5996 EndZ=0
    g13: LineSegment StartX=43.5508 StartY=-35.9996 StartZ=0 EndX=49.1508 EndY=-35.9996 EndZ=0
    g14: LineSegment StartX=49.1508 StartY=-35.9996 StartZ=0 EndX=49.1508 EndY=-39.9996 EndZ=0
    g15: ArcOfCircle CenterX=43.5508 CenterY=-39.9996 CenterZ=0 NormalX=0 NormalY=0 NormalZ=1 AngleXU=0 Radius=5.59996 StartAngle=4.71239 EndAngle=6.28319
    g16: LineSegment StartX=39.5508 StartY=39.1464 StartZ=0 EndX=39.5508 EndY=33.5498 EndZ=0
    g17: ArcOfCircle CenterX=43.5508 CenterY=33.5498 CenterZ=0 NormalX=0 NormalY=0 NormalZ=1 AngleXU=0 Radius=4 StartAngle=3.14158 EndAngle=4.7124
    g18: LineSegment StartX=43.5508 StartY=29.5498 StartZ=0 EndX=49.1508 EndY=29.5498 EndZ=0
    g19: LineSegment StartX=49.1508 StartY=29.5498 StartZ=0 EndX=49.1508 EndY=33.5464 EndZ=0
    g20: ArcOfCircle CenterX=43.5508 CenterY=33.5464 CenterZ=0 NormalX=0 NormalY=0 NormalZ=1 AngleXU=0 Radius=5.59996 StartAngle=0 EndAngle=1.5708
    g21: LineSegment StartX=39.5508 StartY=39.1464 StartZ=0 EndX=43.5508 EndY=39.1464 EndZ=0
    g22: ArcOfCircle CenterX=-49.9492 CenterY=-39.9996 CenterZ=0 NormalX=0 NormalY=0 NormalZ=1 AngleXU=0 Radius=4 StartAngle=-1.8e-15 EndAngle=1.5708
    g23: LineSegment StartX=-45.9492 StartY=-39.9996 StartZ=0 EndX=-45.9492 EndY=-45.5996 EndZ=0
    g24: LineSegment StartX=39.5508 StartY=-45.5996 StartZ=0 EndX=39.5508 EndY=-39.9996 EndZ=0
    g25: ArcOfCircle CenterX=43.5508 CenterY=-39.9996 CenterZ=0 NormalX=0 NormalY=0 NormalZ=1 AngleXU=0 Radius=4 StartAngle=1.5708 EndAngle=3.14159
  constraints (66):
    c: PointOnObject(g0,g-7)
    c: Horizontal(g0)
    c: Tangent(g0,g1) = -1.5708
    c: Coincident(g1,g2)
    c: Vertical(g2)
    c: Coincident(g2,g3)
    c: Coincident(g3,g-9)
    c: Tangent(g3,g4) = -1.5708
    c: Coincident(g4,g-8)
    c: Tangent(g4,g5) = -1.5708
    c: Coincident(g1,g4)
    c: DistanceY(g0,g1) = 4
    c: PointOnObject(g10,g-13)
    c: Horizontal(g6)
    c: Coincident(g7,g-14)
    c: Coincident(g7,g-7)
    c: Coincident(g6,g8)
    c: Coincident(g8,g7)
    c: Tangent(g8,g9) = -1.5708
    c: Coincident(g9,g-14)
    c: Tangent(g9,g10) = -1.5708
    c: DistanceY(g9,g6) = 4
    c: Coincident(g5,g0)
    c: Coincident(g11,g-11)
    c: Coincident(g11,g-12)
    c: Coincident(g-13,g12)
    c: PointOnObject(g12,g-13)
    c: Horizontal(g13)
    c: Coincident(g13,g14)
    c: Tangent(g14,g15) = 1.5708
    c: Coincident(g15,g12)
    c: Coincident(g14,g11)
    c: PointOnObject(g13,g11)
    c: Coincident(g17,g18)
    c: DistanceY(g17,g17) = 4
    c: DistanceX(g16,g17) = 4
    c: Coincident(g20,g19)
    c: Coincident(g19,g-11)
    c: Coincident(g20,g-10)
    c: Coincident(g20,g21)
    c: Horizontal(g21)
    c: PointOnObject(g16,g-9)
    c: Coincident(g21,g16)
    c: Coincident(g17,g-4)
    c: Horizontal(g18)
    c: PointOnObject(g18,g-11)
    c: Coincident(g18,g19)
    c: Coincident(g16,g17)
    c: Vertical(g16)
    c: Vertical(g17,g20)
    c: Horizontal(g1,g1)
    c: Coincident(g22,g6)
    c: Coincident(g23,g22)
    c: Coincident(g23,g10)
    c: Vertical(g23)
    c: DistanceX(g9,g22) = 4
    c: Coincident(g22,g9)
    c: Horizontal(g22,g-14)
    c: Coincident(g24,g12)
    c: Vertical(g24)
    c: DistanceX(g24,g15) = 4
    c: Coincident(g25,g15)
    c: Coincident(g25,g24)
    c: Coincident(g25,g13)
    c: Horizontal(g15,g24)
    c: Vertical(g13,g15)
FEATURE [PartDesign::Pad] Pad005
  BaseFeature = -> Pocket009
  Direction = (0,-1e-16,-1)
  Length = 15
  Length2 = 10
  Profile = -> Sketch015
  ReferenceAxis = -> Sketch015 [N_Axis]
  Refine = true
  Reversed = true
  SideType = 0
  Suppressed = false
  Type = 1
  Type2 = 0
FEATURE [Sketcher::SketchObject] Sketch025
  ArcFitTolerance = 1e-06
  ExternalTypes = [0]
  FullyConstrained = false
  MakeInternals = false
  MapMode = 5
  Placement = pos=(-2.8e-14,47.1996,1.079e-13) rot=(0,0.707107,0.707107;3.14159rad)
  _ExternalGeoVersion = 0
  sketch-geometry (6):
    g0: ArcOfCircle CenterX=-26.1622 CenterY=13.1501 CenterZ=0 NormalX=0 NormalY=0 NormalZ=1 AngleXU=0 Radius=1 StartAngle=5.7277 EndAngle=8.86929
    g1: ArcOfCircle CenterX=-35.1622 CenterY=-1.3502 CenterZ=0 NormalX=0 NormalY=0 NormalZ=1 AngleXU=0 Radius=1 StartAngle=2.58611 EndAngle=5.7277
    g2: LineSegment StartX=-25.3126 StartY=12.6227 StartZ=0 EndX=-34.3126 EndY=-1.87755 EndZ=0
    g3: LineSegment StartX=-27.0118 StartY=13.6775 StartZ=0 EndX=-36.0118 EndY=-0.822843 EndZ=0
    g4: LineSegment [constr] StartX=-35.1622 StartY=-1.3502 StartZ=0 EndX=-35.1622 EndY=-5.3502 EndZ=0
    g5: LineSegment [constr] StartX=-26.1622 StartY=13.1501 StartZ=0 EndX=-26.1622 EndY=18.6498 EndZ=0
  constraints (14):
    c: Tangent(g0,g2) = 1.5708
    c: Tangent(g0,g3) = -1.5708
    c: Tangent(g1,g2) = 1.5708
    c: Tangent(g1,g3) = -1.5708
    c: Radius(g0) = 1
    c: Coincident(g4,g1)
    c: PointOnObject(g4,g-4)
    c: Vertical(g4)
    c: DistanceX(g1,g0) = 9
    c: DistanceY(g4,g4) = 4
    c: Coincident(g5,g0)
    c: PointOnObject(g5,g-3)
    c: Vertical(g5)
    c: Parallel(g3,g2)
FEATURE [Sketcher::SketchObject] Sketch027
  ArcFitTolerance = 1e-06
  ExternalTypes = [0]
  FullyConstrained = false
  MakeInternals = false
  MapMode = 5
  Placement = pos=(0,-40.7464,7.21e-14) rot=(1,0,0;1.5708rad)
  _ExternalGeoVersion = 1
  sketch-geometry (5):
    g0: LineSegment StartX=4.44763 StartY=1.1498 StartZ=0 EndX=4.44763 EndY=14.6498 EndZ=0
    g1: LineSegment StartX=4.44763 StartY=14.6498 StartZ=0 EndX=32.4476 EndY=14.6498 EndZ=0
    g2: LineSegment StartX=32.4476 StartY=14.6498 StartZ=0 EndX=32.4476 EndY=1.1498 EndZ=0
    g3: LineSegment StartX=4.44763 StartY=1.1498 StartZ=0 EndX=32.4476 EndY=1.1498 EndZ=0
    g4: LineSegment [constr] StartX=32.4476 StartY=14.6498 StartZ=0 EndX=32.4476 EndY=16.6498 EndZ=0
  constraints (14):
    c: Vertical(g2)
    c: Vertical(g0)
    c: Coincident(g1,g2)
    c: Coincident(g0,g1)
    c: DistanceX(g0,g2) = 28
    c: Horizontal(g3)
    c: Coincident(g3,g0)
    c: Coincident(g3,g2)
    c: DistanceY(g2,g2) = 13.5
    c: Horizontal(g1)
    c: Coincident(g4,g1)
    c: PointOnObject(g4,g-3)
    c: Vertical(g4)
    c: DistanceY(g4,g4) = 2
FEATURE [Sketcher::SketchObject] Sketch029
  ArcFitTolerance = 1e-06
  AttachmentOffset = pos=(0,0,23) rot=(0,0,1;0rad)
  AttachmentSupport = -> [XY_Plane033]
  ExternalTypes = [0]
  FullyConstrained = false
  MakeInternals = false
  MapMode = 5
  Placement = pos=(0,0,23) rot=(0,0,1;0rad)
  _ExternalGeoVersion = 1
  sketch-geometry (8):
    g0: Circle CenterX=-48.6895 CenterY=16.0781 CenterZ=0 NormalX=0 NormalY=0 NormalZ=1 AngleXU=0 Radius=1.875
    g1: Circle CenterX=-48.6895 CenterY=-9.72188 CenterZ=0 NormalX=0 NormalY=0 NormalZ=1 AngleXU=0 Radius=1.875
    g2: Circle CenterX=-22.8895 CenterY=-9.72188 CenterZ=0 NormalX=0 NormalY=0 NormalZ=1 AngleXU=0 Radius=1.875
    g3: Circle CenterX=-22.8895 CenterY=16.0781 CenterZ=0 NormalX=0 NormalY=0 NormalZ=1 AngleXU=0 Radius=1.875
    g4: LineSegment [constr] StartX=-48.6895 StartY=16.0781 StartZ=0 EndX=-48.6895 EndY=-9.72188 EndZ=0
    g5: LineSegment [constr] StartX=-48.6895 StartY=-9.72188 StartZ=0 EndX=-22.8895 EndY=-9.72188 EndZ=0
    g6: LineSegment [constr] StartX=-22.8895 StartY=-9.72188 StartZ=0 EndX=-22.8895 EndY=16.0781 EndZ=0
    g7: LineSegment [constr] StartX=-22.8895 StartY=16.0781 StartZ=0 EndX=-48.6895 EndY=16.0781 EndZ=0
  constraints (18):
    c: Diameter(g0) = 3.75
    c: Coincident(g4,g5)
    c: Coincident(g5,g6)
    c: Coincident(g6,g7)
    c: Coincident(g7,g4)
    c: Vertical(g4)
    c: Vertical(g6)
    c: Horizontal(g5)
    c: Horizontal(g7)
    c: Coincident(g4,g0)
    c: Coincident(g5,g2)
    c: Equal(g4,g7)
    c: DistanceY(g4,g4) = 25.8
    c: Coincident(g4,g1)
    c: Coincident(g6,g3)
    c: Equal(g0,g3)
    c: Equal(g0,g2)
    c: Equal(g0,g1)
FEATURE [Sketcher::SketchObject] Sketch030
  ArcFitTolerance = 1e-06
  AttachmentOffset = pos=(-43,-4,0) rot=(0,0,1;0rad)
  AttachmentSupport = -> [Pad004]
  ExternalGeometry = -> [Pad004]
  ExternalTypes = [0,0]
  FullyConstrained = false
  MakeInternals = false
  MapMode = 5
  Placement = pos=(-43,4,16.6498) rot=(1,0,0;3.14159rad)
  _ExternalGeoVersion = 1
  sketch-geometry (122):
    g0: LineSegment StartX=-1.37665 StartY=0.773405 StartZ=0 EndX=-2.87666 EndY=3.37148 EndZ=0
    g1: LineSegment StartX=-2.87666 StartY=3.37148 StartZ=0 EndX=-5.87666 EndY=3.37147 EndZ=0
    g2: LineSegment StartX=-5.87666 StartY=3.37147 StartZ=0 EndX=-7.37665 EndY=0.773389 EndZ=0
    g3: LineSegment StartX=-7.37665 StartY=0.773389 StartZ=0 EndX=-5.87665 EndY=-1.82468 EndZ=0
    g4: LineSegment StartX=-5.87665 StartY=-1.82468 StartZ=0 EndX=-2.87665 EndY=-1.82467 EndZ=0
    g5: LineSegment StartX=-2.87665 StartY=-1.82467 StartZ=0 EndX=-1.37665 EndY=0.773405 EndZ=0
    g6: Circle [constr] CenterX=-4.37665 CenterY=0.773397 CenterZ=0 NormalX=0 NormalY=0 NormalZ=1 AngleXU=0 Radius=3
    g7: LineSegment StartX=4.42238 StartY=4.12149 StartZ=0 EndX=2.92237 EndY=6.71957 EndZ=0
    g8: LineSegment StartX=2.92237 StartY=6.71957 StartZ=0 EndX=-0.07763 EndY=6.71956 EndZ=0
    g9: LineSegment StartX=-0.07763 StartY=6.71956 StartZ=0 EndX=-1.57762 EndY=4.12148 EndZ=0
    g10: LineSegment StartX=-1.57762 StartY=4.12148 StartZ=0 EndX=-0.0776162 EndY=1.52341 EndZ=0
    g11: LineSegment StartX=-0.0776162 StartY=1.52341 StartZ=0 EndX=2.92238 EndY=1.52341 EndZ=0
    g12: LineSegment StartX=2.92238 StartY=1.52341 StartZ=0 EndX=4.42238 EndY=4.12149 EndZ=0
    g13: Circle [constr] CenterX=1.42238 CenterY=4.12149 CenterZ=0 NormalX=0 NormalY=0 NormalZ=1 AngleXU=0 Radius=3
    g14: LineSegment [constr] StartX=-0.0776162 StartY=1.52341 StartZ=0 EndX=-0.0776162 EndY=0.0234053 EndZ=0
    g15: LineSegment [constr] StartX=-0.0776162 StartY=0.0234053 StartZ=0 EndX=-1.37665 EndY=0.773405 EndZ=0
    g16: LineSegment [constr] StartX=-1.37665 StartY=0.773405 StartZ=0 EndX=-0.0776162 EndY=1.52341 EndZ=0
    g17: Circle [constr] CenterX=-4.37664 CenterY=-5.92275 CenterZ=0 NormalX=0 NormalY=0 NormalZ=1 AngleXU=0 Radius=3
    g18: LineSegment StartX=-2.87665 StartY=-3.32467 StartZ=0 EndX=-5.87665 EndY=-3.32468 EndZ=0
    g19: LineSegment StartX=-1.37664 StartY=-5.92275 StartZ=0 EndX=-2.87665 EndY=-3.32467 EndZ=0
    g20: LineSegment StartX=-2.87663 StartY=-8.52083 StartZ=0 EndX=-1.37664 EndY=-5.92275 EndZ=0
    g21: LineSegment StartX=-5.87663 StartY=-8.52083 StartZ=0 EndX=-2.87663 EndY=-8.52083 EndZ=0
    g22: LineSegment StartX=-7.37664 StartY=-5.92276 StartZ=0 EndX=-5.87663 EndY=-8.52083 EndZ=0
    g23: LineSegment StartX=-5.87665 StartY=-3.32468 StartZ=0 EndX=-7.37664 EndY=-5.92276 EndZ=0
    g24: LineSegment StartX=4.42239 StartY=-2.57466 StartZ=0 EndX=2.92238 EndY=0.0234131 EndZ=0
    g25: LineSegment StartX=2.92238 StartY=0.0234131 StartZ=0 EndX=-0.0776162 EndY=0.0234053 EndZ=0
    g26: LineSegment StartX=-0.0776162 StartY=0.0234053 StartZ=0 EndX=-1.57761 EndY=-2.57467 EndZ=0
    g27: LineSegment StartX=-1.57761 StartY=-2.57467 StartZ=0 EndX=-0.0776026 EndY=-5.17275 EndZ=0
    g28: LineSegment StartX=-0.0776026 StartY=-5.17275 StartZ=0 EndX=2.9224 EndY=-5.17274 EndZ=0
    g29: LineSegment StartX=2.9224 StartY=-5.17274 StartZ=0 EndX=4.42239 EndY=-2.57466 EndZ=0
    g30: Circle [constr] CenterX=1.42239 CenterY=-2.57467 CenterZ=0 NormalX=0 NormalY=0 NormalZ=1 AngleXU=0 Radius=3
    g31: LineSegment [constr] StartX=-0.0776026 StartY=-5.17275 StartZ=0 EndX=-0.0776026 EndY=-6.67275 EndZ=0
    g32: LineSegment [constr] StartX=-0.0776026 StartY=-6.67275 StartZ=0 EndX=-1.37664 EndY=-5.92275 EndZ=0
    g33: LineSegment [constr] StartX=-1.37664 StartY=-5.92275 StartZ=0 EndX=-0.0776026 EndY=-5.17275 EndZ=0
    g34: LineSegment StartX=4.4224 StartY=-9.27082 StartZ=0 EndX=2.9224 EndY=-6.67274 EndZ=0
    g35: LineSegment StartX=2.9224 StartY=-6.67274 StartZ=0 EndX=-0.0776026 EndY=-6.67275 EndZ=0
    g36: LineSegment StartX=-0.0776026 StartY=-6.67275 StartZ=0 EndX=-1.5776 EndY=-9.27083 EndZ=0
    g37: LineSegment StartX=-1.5776 StartY=-9.27083 StartZ=0 EndX=-0.0775954 EndY=-11.8689 EndZ=0
    g38: LineSegment StartX=-0.0775954 StartY=-11.8689 StartZ=0 EndX=2.9224 EndY=-11.8689 EndZ=0
    g39: LineSegment StartX=2.9224 StartY=-11.8689 StartZ=0 EndX=4.4224 EndY=-9.27082 EndZ=0
    g40: Circle [constr] CenterX=1.4224 CenterY=-9.27082 CenterZ=0 NormalX=0 NormalY=0 NormalZ=1 AngleXU=0 Radius=3
    g41: LineSegment StartX=-1.37667 StartY=7.46956 StartZ=0 EndX=-2.87667 EndY=10.0676 EndZ=0
    g42: LineSegment StartX=-2.87667 StartY=10.0676 StartZ=0 EndX=-5.87667 EndY=10.0676 EndZ=0
    g43: LineSegment StartX=-5.87667 StartY=10.0676 StartZ=0 EndX=-7.37667 EndY=7.46954 EndZ=0
    g44: LineSegment StartX=-7.37667 StartY=7.46954 StartZ=0 EndX=-5.87666 EndY=4.87147 EndZ=0
    g45: LineSegment StartX=-5.87666 StartY=4.87147 StartZ=0 EndX=-2.87666 EndY=4.87148 EndZ=0
    g46: LineSegment StartX=-2.87666 StartY=4.87148 StartZ=0 EndX=-1.37667 EndY=7.46956 EndZ=0
    g47: Circle [constr] CenterX=-4.37667 CenterY=7.46955 CenterZ=0 NormalX=0 NormalY=0 NormalZ=1 AngleXU=0 Radius=3
    g48: LineSegment StartX=4.42237 StartY=10.8176 StartZ=0 EndX=2.92237 EndY=13.4157 EndZ=0
    g49: LineSegment StartX=2.92237 StartY=13.4157 StartZ=0 EndX=-0.07763 EndY=13.4157 EndZ=0
    g50: LineSegment StartX=-0.07763 StartY=13.4157 StartZ=0 EndX=-1.57763 EndY=10.8176 EndZ=0
    g51: LineSegment StartX=-1.57763 StartY=10.8176 StartZ=0 EndX=-0.07763 EndY=8.21956 EndZ=0
    g52: LineSegment StartX=-0.07763 StartY=8.21956 StartZ=0 EndX=2.92237 EndY=8.21956 EndZ=0
    g53: LineSegment StartX=2.92237 StartY=8.21956 StartZ=0 EndX=4.42237 EndY=10.8176 EndZ=0
    g54: Circle [constr] CenterX=1.42237 CenterY=10.8176 CenterZ=0 NormalX=0 NormalY=0 NormalZ=1 AngleXU=0 Radius=3
    g55: LineSegment [constr] StartX=-0.07763 StartY=8.21956 StartZ=0 EndX=-0.07763 EndY=6.71956 EndZ=0
    g56: LineSegment [constr] StartX=-0.07763 StartY=6.71956 StartZ=0 EndX=-1.37667 EndY=7.46956 EndZ=0
    g57: LineSegment [constr] StartX=-1.37667 StartY=7.46956 StartZ=0 EndX=-0.07763 EndY=8.21956 EndZ=0
    g58: LineSegment StartX=10.2214 StartY=7.46958 StartZ=0 EndX=8.7214 EndY=10.0677 EndZ=0
    g59: LineSegment StartX=8.7214 StartY=10.0677 StartZ=0 EndX=5.7214 EndY=10.0676 EndZ=0
    g60: LineSegment StartX=5.7214 StartY=10.0676 StartZ=0 EndX=4.22141 EndY=7.46956 EndZ=0
    g61: LineSegment StartX=4.22141 StartY=7.46956 StartZ=0 EndX=5.72142 EndY=4.87149 EndZ=0
    g62: LineSegment StartX=5.72142 StartY=4.87149 StartZ=0 EndX=8.72142 EndY=4.8715 EndZ=0
    g63: LineSegment StartX=8.72142 StartY=4.8715 StartZ=0 EndX=10.2214 EndY=7.46958 EndZ=0
    g64: Circle [constr] CenterX=7.22141 CenterY=7.46957 CenterZ=0 NormalX=0 NormalY=0 NormalZ=1 AngleXU=0 Radius=3
    g65: LineSegment StartX=10.2214 StartY=0.773419 StartZ=0 EndX=8.72142 EndY=3.37149 EndZ=0
    g66: LineSegment StartX=8.72142 StartY=3.37149 StartZ=0 EndX=5.72142 EndY=3.37149 EndZ=0
    g67: LineSegment StartX=5.72142 StartY=3.37149 StartZ=0 EndX=4.22142 EndY=0.773413 EndZ=0
    g68: LineSegment StartX=4.22142 StartY=0.773413 StartZ=0 EndX=5.72142 EndY=-1.82466 EndZ=0
    g69: LineSegment StartX=5.72142 StartY=-1.82466 StartZ=0 EndX=8.72142 EndY=-1.82466 EndZ=0
    g70: LineSegment StartX=8.72142 StartY=-1.82466 StartZ=0 EndX=10.2214 EndY=0.773419 EndZ=0
    g71: Circle [constr] CenterX=7.22142 CenterY=0.773416 CenterZ=0 NormalX=0 NormalY=0 NormalZ=1 AngleXU=0 Radius=3
    g72: Circle [constr] CenterX=7.22143 CenterY=-5.92273 CenterZ=0 NormalX=0 NormalY=0 NormalZ=1 AngleXU=0 Radius=3
    g73: LineSegment StartX=8.72142 StartY=-3.32465 StartZ=0 EndX=5.72142 EndY=-3.32466 EndZ=0
    g74: LineSegment StartX=10.2214 StartY=-5.92272 StartZ=0 EndX=8.72142 EndY=-3.32465 EndZ=0
    g75: LineSegment StartX=8.72144 StartY=-8.5208 StartZ=0 EndX=10.2214 EndY=-5.92272 EndZ=0
    g76: LineSegment StartX=5.72144 StartY=-8.52081 StartZ=0 EndX=8.72144 EndY=-8.5208 EndZ=0
    g77: LineSegment StartX=4.22143 StartY=-5.92274 StartZ=0 EndX=5.72144 EndY=-8.52081 EndZ=0
    g78: LineSegment StartX=5.72142 StartY=-3.32466 StartZ=0 EndX=4.22143 EndY=-5.92274 EndZ=0
    g79: LineSegment [constr] StartX=4.22143 StartY=-5.92274 StartZ=0 EndX=2.9224 EndY=-6.67274 EndZ=0
    g80: LineSegment [constr] StartX=2.9224 StartY=-6.67274 StartZ=0 EndX=2.9224 EndY=-5.17274 EndZ=0
    g81: LineSegment [constr] StartX=2.9224 StartY=-5.17274 StartZ=0 EndX=4.22143 EndY=-5.92274 EndZ=0
    g82: LineSegment [constr] StartX=4.22142 StartY=0.773413 StartZ=0 EndX=2.92238 EndY=0.0234131 EndZ=0
    g83: LineSegment [constr] StartX=2.92238 StartY=0.0234131 StartZ=0 EndX=2.92238 EndY=1.52341 EndZ=0
    g84: LineSegment [constr] StartX=2.92238 StartY=1.52341 StartZ=0 EndX=4.22142 EndY=0.773413 EndZ=0
    g85: LineSegment [constr] StartX=4.22141 StartY=7.46956 StartZ=0 EndX=2.92237 EndY=6.71957 EndZ=0
    g86: LineSegment [constr] StartX=2.92237 StartY=6.71957 StartZ=0 EndX=2.92237 EndY=8.21956 EndZ=0
    g87: LineSegment [constr] StartX=2.92237 StartY=8.21956 StartZ=0 EndX=4.22141 EndY=7.46956 EndZ=0
    g88: LineSegment [constr] StartX=-4.37665 StartY=0.773397 StartZ=0 EndX=-6.94923 EndY=43.1464 EndZ=0
    g89: LineSegment [constr] StartX=-4.37665 StartY=0.773397 StartZ=0 EndX=-6.94923 EndY=-41.5996 EndZ=0
    g90: LineSegment [constr] StartX=-1.57761 StartY=-2.57467 StartZ=0 EndX=-2.87665 EndY=-1.82467 EndZ=0
    g91: LineSegment [constr] StartX=-2.87665 StartY=-3.32467 StartZ=0 EndX=-2.87665 EndY=-1.82467 EndZ=0
    g92: LineSegment [constr] StartX=-1.57761 StartY=-2.57467 StartZ=0 EndX=-2.87665 EndY=-3.32467 EndZ=0
    g93: LineSegment [constr] StartX=-1.57762 StartY=4.12148 StartZ=0 EndX=-2.87666 EndY=4.87148 EndZ=0
    g94: LineSegment [constr] StartX=-2.87666 StartY=4.87148 StartZ=0 EndX=-2.87666 EndY=3.37148 EndZ=0
    g95: LineSegment [constr] StartX=-2.87666 StartY=3.37148 StartZ=0 EndX=-1.57762 EndY=4.12148 EndZ=0
    g96: LineSegment [constr] StartX=5.72142 StartY=4.87149 StartZ=0 EndX=4.42238 EndY=4.12149 EndZ=0
    g97: LineSegment [constr] StartX=4.42238 StartY=4.12149 StartZ=0 EndX=5.72142 EndY=3.37149 EndZ=0
    g98: LineSegment [constr] StartX=5.72142 StartY=3.37149 StartZ=0 EndX=5.72142 EndY=4.87149 EndZ=0
    g99: LineSegment [constr] StartX=5.72142 StartY=-3.32466 StartZ=0 EndX=5.72142 EndY=-1.82466 EndZ=0
    g100: LineSegment [constr] StartX=5.72142 StartY=-1.82466 StartZ=0 EndX=4.42239 EndY=-2.57466 EndZ=0
    g101: LineSegment [constr] StartX=4.42239 StartY=-2.57466 StartZ=0 EndX=5.72142 EndY=-3.32466 EndZ=0
    g102: LineSegment StartX=10.2214 StartY=-12.6189 StartZ=0 EndX=8.72144 EndY=-10.0208 EndZ=0
    g103: LineSegment StartX=8.72144 StartY=-10.0208 StartZ=0 EndX=5.72144 EndY=-10.0208 EndZ=0
    g104: LineSegment StartX=5.72144 StartY=-10.0208 StartZ=0 EndX=4.22144 EndY=-12.6189 EndZ=0
    g105: LineSegment StartX=4.22144 StartY=-12.6189 StartZ=0 EndX=5.72144 EndY=-15.217 EndZ=0
    g106: LineSegment StartX=5.72144 StartY=-15.217 StartZ=0 EndX=8.72144 EndY=-15.217 EndZ=0
    g107: LineSegment StartX=8.72144 StartY=-15.217 StartZ=0 EndX=10.2214 EndY=-12.6189 EndZ=0
    g108: Circle [constr] CenterX=7.22144 CenterY=-12.6189 CenterZ=0 NormalX=0 NormalY=0 NormalZ=1 AngleXU=0 Radius=3
    g109: LineSegment StartX=10.2214 StartY=14.1657 StartZ=0 EndX=8.7214 EndY=16.7638 EndZ=0
    g110: LineSegment StartX=8.7214 StartY=16.7638 StartZ=0 EndX=5.7214 EndY=16.7638 EndZ=0
    g111: LineSegment StartX=5.7214 StartY=16.7638 StartZ=0 EndX=4.2214 EndY=14.1657 EndZ=0
    g112: LineSegment StartX=4.2214 StartY=14.1657 StartZ=0 EndX=5.7214 EndY=11.5676 EndZ=0
    g113: LineSegment StartX=5.7214 StartY=11.5676 StartZ=0 EndX=8.7214 EndY=11.5676 EndZ=0
    g114: LineSegment StartX=8.7214 StartY=11.5676 StartZ=0 EndX=10.2214 EndY=14.1657 EndZ=0
    g115: Circle [constr] CenterX=7.2214 CenterY=14.1657 CenterZ=0 NormalX=0 NormalY=0 NormalZ=1 AngleXU=0 Radius=3
    g116: LineSegment [constr] StartX=5.7214 StartY=10.0676 StartZ=0 EndX=5.7214 EndY=11.5676 EndZ=0
    g117: LineSegment [constr] StartX=5.7214 StartY=11.5676 StartZ=0 EndX=4.42237 EndY=10.8176 EndZ=0
    g118: LineSegment [constr] StartX=4.42237 StartY=10.8176 StartZ=0 EndX=5.7214 EndY=10.0676 EndZ=0
    g119: LineSegment [constr] StartX=4.4224 StartY=-9.27082 StartZ=0 EndX=5.72144 EndY=-10.0208 EndZ=0
    g120: LineSegment [constr] StartX=5.72144 StartY=-10.0208 StartZ=0 EndX=5.72144 EndY=-8.52081 EndZ=0
    g121: LineSegment [constr] StartX=5.72144 StartY=-8.52081 StartZ=0 EndX=4.4224 EndY=-9.27082 EndZ=0
  constraints (295):
    c: Coincident(g0,g1)
    c: Coincident(g1,g2)
    c: Coincident(g2,g3)
    c: Coincident(g3,g4)
    c: Coincident(g4,g5)
    c: Coincident(g5,g0)
    c: Equal(g0, g1-g5) x5
    c: PointOnObject(g0,g6)
    c: PointOnObject(g1,g6)
    c: PointOnObject(g2,g6)
    c: PointOnObject(g3,g6)
    c: PointOnObject(g4,g6)
    c: PointOnObject(g5,g6)
    c: Radius(g6) = 3
    c: Coincident(g7,g8)
    c: Coincident(g8,g9)
    c: Coincident(g9,g10)
    c: Coincident(g10,g11)
    c: Coincident(g11,g12)
    c: Coincident(g12,g7)
    c: Equal(g7, g8-g12) x5
    c: PointOnObject(g7,g13)
    c: PointOnObject(g8,g13)
    c: PointOnObject(g9,g13)
    c: PointOnObject(g10,g13)
    c: PointOnObject(g11,g13)
    c: PointOnObject(g12,g13)
    c: Radius(g13) = 3
    c: Coincident(g10,g14)
    c: Coincident(g14,g15)
    c: Coincident(g15,g0)
    c: Coincident(g15,g16)
    c: Coincident(g16,g14)
    c: Equal(g14,g15)
    c: Equal(g14,g16)
    c: Distance(g0,g10) = 1.5
    c: Coincident(g19,g18)
    c: Coincident(g18,g23)
    c: Coincident(g23,g22)
    c: Coincident(g22,g21)
    c: Coincident(g21,g20)
    c: Coincident(g20,g19)
    c: Equal(g19,g18)
    c: Equal(g19,g23)
    c: Equal(g19,g22)
    c: Equal(g19,g21)
    c: Equal(g19,g20)
    c: PointOnObject(g19,g17)
    c: PointOnObject(g18,g17)
    c: PointOnObject(g23,g17)
    c: PointOnObject(g22,g17)
    c: PointOnObject(g21,g17)
    c: PointOnObject(g20,g17)
    c: Radius(g17) = 3
    c: Coincident(g24,g25)
    c: Coincident(g34,g35)
    c: Coincident(g25,g26)
    c: Coincident(g35,g36)
    c: Coincident(g26,g27)
    c: Coincident(g36,g37)
    c: Coincident(g27,g28)
    c: Coincident(g37,g38)
    c: Coincident(g28,g29)
    c: Coincident(g38,g39)
    c: Coincident(g29,g24)
    c: Coincident(g39,g34)
    c: Equal(g24,g25)
    c: Equal(g34,g35)
    c: Equal(g24,g26)
    c: Equal(g34,g36)
    c: Equal(g24,g27)
    c: Equal(g34,g37)
    c: Equal(g24,g28)
    c: Equal(g34,g38)
    c: Equal(g24,g29)
    c: Equal(g34,g39)
    c: PointOnObject(g24,g30)
    c: PointOnObject(g34,g40)
    c: PointOnObject(g25,g30)
    c: PointOnObject(g35,g40)
    c: PointOnObject(g26,g30)
    c: PointOnObject(g36,g40)
    c: PointOnObject(g27,g30)
    c: PointOnObject(g37,g40)
    c: PointOnObject(g28,g30)
    c: PointOnObject(g38,g40)
    c: PointOnObject(g29,g30)
    c: PointOnObject(g39,g40)
    c: Radius(g30) = 3
    c: Radius(g40) = 3
    c: Coincident(g27,g31)
    c: Coincident(g31,g32)
    c: Coincident(g32,g19)
    c: Coincident(g32,g33)
    c: Coincident(g33,g31)
    c: Equal(g31,g32)
    c: Equal(g31,g33)
    c: Distance(g19,g27) = 1.5
    c: Coincident(g25,g14)
    c: Coincident(g31,g35)
    c: Coincident(g41,g42)
    c: Coincident(g42,g43)
    c: Coincident(g43,g44)
    c: Coincident(g44,g45)
    c: Coincident(g45,g46)
    c: Coincident(g46,g41)
    c: Equal(g41, g42-g46) x5
    c: PointOnObject(g41,g47)
    c: PointOnObject(g42,g47)
    c: PointOnObject(g43,g47)
    c: PointOnObject(g44,g47)
    c: PointOnObject(g45,g47)
    c: PointOnObject(g46,g47)
    c: Radius(g47) = 3
    c: Coincident(g48,g49)
    c: Coincident(g49,g50)
    c: Coincident(g50,g51)
    c: Coincident(g51,g52)
    c: Coincident(g52,g53)
    c: Coincident(g53,g48)
    c: Equal(g48, g49-g53) x5
    c: PointOnObject(g48,g54)
    c: PointOnObject(g49,g54)
    c: PointOnObject(g50,g54)
    c: PointOnObject(g51,g54)
    c: PointOnObject(g52,g54)
    c: PointOnObject(g53,g54)
    c: Radius(g54) = 3
    c: Coincident(g51,g55)
    c: Coincident(g55,g56)
    c: Coincident(g56,g41)
    c: Coincident(g56,g57)
    c: Coincident(g57,g55)
    c: Equal(g55,g56)
    c: Equal(g55,g57)
    c: Distance(g41,g51) = 1.5
    c: Coincident(g55,g8)
    c: Coincident(g58,g59)
    c: Coincident(g59,g60)
    c: Coincident(g60,g61)
    c: Coincident(g61,g62)
    c: Coincident(g62,g63)
    c: Coincident(g63,g58)
    c: Equal(g58, g59-g63) x5
    c: PointOnObject(g58,g64)
    c: PointOnObject(g59,g64)
    c: PointOnObject(g60,g64)
    c: PointOnObject(g61,g64)
    c: PointOnObject(g62,g64)
    c: PointOnObject(g63,g64)
    c: Radius(g64) = 3
    c: Coincident(g65,g66)
    c: Coincident(g66,g67)
    c: Coincident(g67,g68)
    c: Coincident(g68,g69)
    c: Coincident(g69,g70)
    c: Coincident(g70,g65)
    c: Equal(g65, g66-g70) x5
    c: PointOnObject(g65,g71)
    c: PointOnObject(g66,g71)
    c: PointOnObject(g67,g71)
    c: PointOnObject(g68,g71)
    c: PointOnObject(g69,g71)
    c: PointOnObject(g70,g71)
    c: Radius(g71) = 3
    c: Coincident(g74,g73)
    c: Coincident(g73,g78)
    c: Coincident(g78,g77)
    c: Coincident(g77,g76)
    c: Coincident(g76,g75)
    c: Coincident(g75,g74)
    c: Equal(g74,g73)
    c: Equal(g74,g78)
    c: Equal(g74,g77)
    c: Equal(g74,g76)
    c: Equal(g74,g75)
    c: PointOnObject(g74,g72)
    c: PointOnObject(g73,g72)
    c: PointOnObject(g78,g72)
    c: PointOnObject(g77,g72)
    c: PointOnObject(g76,g72)
    c: PointOnObject(g75,g72)
    c: Radius(g72) = 3
    c: Coincident(g77,g79)
    c: Coincident(g79,g34)
    c: Coincident(g79,g80)
    c: Coincident(g80,g28)
    c: Coincident(g80,g81)
    c: Coincident(g81,g79)
    c: Equal(g32,g79)
    c: Equal(g79,g81)
    c: Coincident(g67,g82)
    c: Coincident(g82,g24)
    c: Coincident(g82,g83)
    c: Coincident(g83,g11)
    c: Coincident(g83,g84)
    c: Coincident(g84,g82)
    c: Equal(g15,g82)
    c: Equal(g82,g84)
    c: Coincident(g60,g85)
    c: Coincident(g85,g7)
    c: Coincident(g85,g86)
    c: Coincident(g86,g52)
    c: Coincident(g86,g87)
    c: Coincident(g87,g85)
    c: Equal(g82,g85)
    c: Equal(g84,g87)
    c: Coincident(g88,g6)
    c: Coincident(g88,g-3)
    c: Coincident(g89,g6)
    c: Coincident(g89,g-4)
    c: Equal(g88,g89)
    c: Vertical(g14)
    c: Vertical(g31)
    c: Vertical(g86)
    c: Vertical(g55)
    c: Vertical(g83)
    c: Vertical(g80)
    c: Coincident(g90,g26)
    c: Coincident(g90,g4)
    c: Coincident(g91,g18)
    c: Coincident(g91,g4)
    c: Coincident(g92,g26)
    c: Coincident(g92,g18)
    c: Coincident(g93,g9)
    c: Coincident(g93,g45)
    c: Coincident(g94,g45)
    c: Coincident(g94,g0)
    c: Coincident(g95,g0)
    c: Coincident(g95,g9)
    c: Vertical(g94)
    c: Vertical(g91)
    c: Equal(g55,g94)
    c: Horizontal(g52)
    c: Coincident(g61,g96)
    c: Coincident(g96,g7)
    c: Coincident(g96,g97)
    c: Coincident(g97,g66)
    c: Coincident(g97,g98)
    c: Coincident(g98,g96)
    c: Vertical(g98)
    c: Equal(g55,g98)
    c: Coincident(g73,g99)
    c: Coincident(g99,g68)
    c: Vertical(g99)
    c: Coincident(g99,g100)
    c: Coincident(g100,g24)
    c: Coincident(g100,g101)
    c: Coincident(g101,g99)
    c: Coincident(g102,g103)
    c: Coincident(g103,g104)
    c: Coincident(g104,g105)
    c: Coincident(g105,g106)
    c: Coincident(g106,g107)
    c: Coincident(g107,g102)
    c: Equal(g102, g103-g107) x5
    c: PointOnObject(g102,g108)
    c: PointOnObject(g103,g108)
    c: PointOnObject(g104,g108)
    c: PointOnObject(g105,g108)
    c: PointOnObject(g106,g108)
    c: PointOnObject(g107,g108)
    c: Radius(g108) = 3
    c: Coincident(g109,g110)
    c: Coincident(g110,g111)
    c: Coincident(g111,g112)
    c: Coincident(g112,g113)
    c: Coincident(g113,g114)
    c: Coincident(g114,g109)
    c: Equal(g109, g110-g114) x5
    c: PointOnObject(g109,g115)
    c: PointOnObject(g110,g115)
    c: PointOnObject(g111,g115)
    c: PointOnObject(g112,g115)
    c: PointOnObject(g113,g115)
    c: PointOnObject(g114,g115)
    c: Radius(g115) = 3
    c: Coincident(g59,g116)
    c: Coincident(g116,g112)
    c: Coincident(g116,g117)
    c: Coincident(g117,g48)
    c: Coincident(g117,g118)
    c: Coincident(g118,g116)
    c: Vertical(g116)
    c: Equal(g87,g117)
    c: Coincident(g34,g119)
    c: Coincident(g119,g103)
    c: Coincident(g119,g120)
    c: Coincident(g120,g76)
    c: Coincident(g120,g121)
    c: Coincident(g121,g119)
    c: Equal(g81,g120)
    c: Equal(g81,g119)
    c: Horizontal(g103)
    c: Horizontal(g113)
FEATURE [Sketcher::SketchObject] Sketch031
  ArcFitTolerance = 1e-06
  ExternalTypes = [0]
  FullyConstrained = false
  MakeInternals = false
  MapMode = 5
  Placement = pos=(0,0,18.6498) rot=(0,0,1;0rad)
  _ExternalGeoVersion = 1
  sketch-geometry (6):
    g0: LineSegment StartX=-57.1492 StartY=32.4113 StartZ=0 EndX=16.7268 EndY=32.4113 EndZ=0
    g1: LineSegment StartX=16.7268 StartY=32.4113 StartZ=0 EndX=16.7268 EndY=-25.9581 EndZ=0
    g2: LineSegment StartX=16.7268 StartY=-25.9581 StartZ=0 EndX=-57.1492 EndY=-25.9581 EndZ=0
    g3: LineSegment StartX=-57.1492 StartY=-25.9581 StartZ=0 EndX=-57.1492 EndY=32.4113 EndZ=0
    g4: LineSegment [constr] StartX=-57.1492 StartY=39.9996 StartZ=0 EndX=-57.1492 EndY=32.4113 EndZ=0
    g5: LineSegment [constr] StartX=-57.1492 StartY=-25.9581 StartZ=0 EndX=-57.1492 EndY=-33.5464 EndZ=0
  constraints (14):
    c: PointOnObject(g0,g-3)
    c: Horizontal(g0)
    c: Coincident(g0,g1)
    c: Vertical(g1)
    c: Coincident(g1,g2)
    c: PointOnObject(g2,g-3)
    c: Horizontal(g2)
    c: Coincident(g2,g3)
    c: Coincident(g3,g0)
    c: Coincident(g4,g-3)
    c: Coincident(g4,g0)
    c: Coincident(g5,g2)
    c: Coincident(g5,g-3)
    c: Equal(g4,g5)
FEATURE [Sketcher::SketchObject] Sketch039
  ArcFitTolerance = 1e-06
  AttachmentOffset = pos=(0,0,-2) rot=(0,0,1;0rad)
  ExternalTypes = [0,0,0,0]
  FullyConstrained = true
  MakeInternals = false
  MapMode = 5
  Placement = pos=(0,30.4113,4e-16) rot=(0,0.707107,0.707107;3.14159rad)
  _ExternalGeoVersion = 1
  sketch-geometry (4):
    g0: LineSegment StartX=-16.4797 StartY=16.6498 StartZ=0 EndX=31.3391 EndY=28.6498 EndZ=0
    g1: LineSegment StartX=31.3391 StartY=28.6498 StartZ=0 EndX=55.5492 EndY=28.6498 EndZ=0
    g2: LineSegment StartX=55.5492 StartY=28.6498 StartZ=0 EndX=55.5492 EndY=16.6498 EndZ=0
    g3: LineSegment StartX=55.5492 StartY=16.6498 StartZ=0 EndX=-16.4797 EndY=16.6498 EndZ=0
  constraints (11):
    c: Coincident(g0,g1)
    c: Horizontal(g1)
    c: Coincident(g1,g2)
    c: Vertical(g2)
    c: Coincident(g2,g3)
    c: Coincident(g3,g0)
    c: Parallel(g0,g-3)
    c: Distance(g0,g-3) = 2
    c: Distance(g1,g-5) = 2
    c: Distance(g-4,g2) = 1.6
    c: Tangent(g3,g-6)
FEATURE [Sketcher::SketchObject] Sketch040
  ArcFitTolerance = 1e-06
  ExternalTypes = [0,0,0,0]
  FullyConstrained = false
  MakeInternals = false
  MapMode = 5
  Placement = pos=(-57.1492,3.75e-14,1.895e-13) rot=(0.57735,-0.57735,-0.57735;2.0944rad)
  _ExternalGeoVersion = 1
  sketch-geometry (18):
    g0: LineSegment StartX=-17.0766 StartY=24.5 StartZ=0 EndX=-17.0766 EndY=4.5 EndZ=0
    g1: LineSegment StartX=-17.0766 StartY=4.5 StartZ=0 EndX=10.6234 EndY=4.5 EndZ=0
    g2: LineSegment StartX=10.6234 StartY=4.5 StartZ=0 EndX=10.6234 EndY=24.5 EndZ=0
    g3: LineSegment StartX=10.6234 StartY=24.5 StartZ=0 EndX=-17.0766 EndY=24.5 EndZ=0
    g4: Circle CenterX=-27.1945 CenterY=7.92829 CenterZ=0 NormalX=0 NormalY=0 NormalZ=1 AngleXU=0 Radius=4
    g5: Circle CenterX=20.7413 CenterY=7.92829 CenterZ=0 NormalX=0 NormalY=0 NormalZ=1 AngleXU=0 Radius=4
    g6: LineSegment [constr] StartX=-32.4113 StartY=30.6498 StartZ=0 EndX=-17.0766 EndY=24.5 EndZ=0
    g7: LineSegment [constr] StartX=10.6234 StartY=24.5 StartZ=0 EndX=25.9581 EndY=30.6498 EndZ=0
    g8: LineSegment [constr] StartX=29.5464 StartY=-1.776e-13 StartZ=0 EndX=-35.9996 EndY=-1.91e-13 EndZ=0
    g9: LineSegment [constr] StartX=10.6234 StartY=4.5 StartZ=0 EndX=29.5464 EndY=-1.776e-13 EndZ=0
    g10: LineSegment [constr] StartX=-17.0766 StartY=4.5 StartZ=0 EndX=-35.9996 EndY=-1.91e-13 EndZ=0
    g11: LineSegment [constr] StartX=-17.0766 StartY=4.5 StartZ=0 EndX=-17.0766 EndY=-1.883e-13 EndZ=0
    g12: LineSegment [constr] StartX=10.6234 StartY=4.5 StartZ=0 EndX=20.7413 EndY=7.92829 EndZ=0
    g13: LineSegment [constr] StartX=20.7413 StartY=7.92829 StartZ=0 EndX=29.5464 EndY=-1.776e-13 EndZ=0
    g14: LineSegment [constr] StartX=20.7413 StartY=7.92829 StartZ=0 EndX=10.6234 EndY=24.5 EndZ=0
    g15: LineSegment [constr] StartX=-17.0766 StartY=4.5 StartZ=0 EndX=-27.1945 EndY=7.92829 EndZ=0
    g16: LineSegment [constr] StartX=-27.1945 StartY=7.92829 StartZ=0 EndX=-35.9996 EndY=-1.91e-13 EndZ=0
    g17: LineSegment [constr] StartX=-27.1945 StartY=7.92829 StartZ=0 EndX=-17.0766 EndY=24.5 EndZ=0
  constraints (41):
    c: Coincident(g0,g1)
    c: Coincident(g1,g2)
    c: Coincident(g2,g3)
    c: Coincident(g3,g0)
    c: Vertical(g0)
    c: Vertical(g2)
    c: Horizontal(g1)
    c: Horizontal(g3)
    c: Diameter(g4) = 8
    c: Diameter(g5) = 8
    c: DistanceY(g0,g0) = 20
    c: DistanceX(g3,g3) = 27.7
    c: Coincident(g6,g-3)
    c: Coincident(g6,g0)
    c: Coincident(g7,g2)
    c: Coincident(g7,g-3)
    c: Equal(g6,g7)
    c: Coincident(g8,g-5)
    c: Coincident(g8,g-4)
    c: Coincident(g9,g1)
    c: Coincident(g9,g8)
    c: Coincident(g10,g0)
    c: Coincident(g10,g8)
    c: Coincident(g11,g0)
    c: PointOnObject(g11,g8)
    c: Vertical(g11)
    c: DistanceY(g11,g11) = 4.5
    c: Coincident(g12,g1)
    c: Coincident(g12,g5)
    c: Coincident(g13,g5)
    c: Coincident(g13,g8)
    c: Coincident(g14,g5)
    c: Coincident(g14,g2)
    c: Coincident(g15,g0)
    c: Coincident(g15,g4)
    c: Coincident(g16,g4)
    c: Coincident(g16,g8)
    c: Coincident(g17,g4)
    c: Coincident(g17,g0)
    c: Equal(g12,g15)
    c: Equal(g16,g13)
FEATURE [Sketcher::SketchObject] Sketch047
  ArcFitTolerance = 1e-06
  AttachmentSupport = -> [Pad005]
  ExternalGeometry = -> [Binder001]
  ExternalTypes = [0,0,0,0]
  FullyConstrained = true
  MakeInternals = false
  MapMode = 5
  Placement = pos=(0,0,-4e-16) rot=(1,0,0;3.14159rad)
  _ExternalGeoVersion = 1
  sketch-geometry (4):
    g0: Circle CenterX=-49.95 CenterY=-40 CenterZ=0 NormalX=0 NormalY=0 NormalZ=1 AngleXU=0 Radius=2.425
    g1: Circle CenterX=-49.9492 CenterY=33.5464 CenterZ=0 NormalX=0 NormalY=0 NormalZ=1 AngleXU=0 Radius=2.425
    g2: Circle CenterX=43.5508 CenterY=33.5498 CenterZ=0 NormalX=0 NormalY=0 NormalZ=1 AngleXU=0 Radius=2.425
    g3: Circle CenterX=43.551 CenterY=-39.9996 CenterZ=0 NormalX=0 NormalY=0 NormalZ=1 AngleXU=0 Radius=2.425
  constraints (8):
    c: Coincident(g0,g-3)
    c: Diameter(g0) = 4.85
    c: Coincident(g1,g-6)
    c: Coincident(g2,g-5)
    c: Coincident(g3,g-4)
    c: Equal(g0,g1)
    c: Equal(g0,g2)
    c: Equal(g0,g3)
FEATURE [PartDesign::Pocket] Pocket024
  BaseFeature = -> Pad005
  Direction = (0,0,1)
  Length = 9
  Length2 = 5
  Profile = -> Sketch047
  ReferenceAxis = -> Sketch047 [N_Axis]
  Refine = true
  SideType = 0
  Suppressed = false
  Type = 0
  Type2 = 0
FEATURE [PartDesign::Pocket] Pocket013
  BaseFeature = -> Pocket024
  Direction = (-1e-16,-1,-2.4e-15)
  Length = 1.6
  Length2 = 5
  Profile = -> Sketch025
  ReferenceAxis = -> Sketch025 [N_Axis]
  Refine = true
  SideType = 0
  Suppressed = false
  Type = 2
  Type2 = 0
FEATURE [PartDesign::LinearPattern] LinearPattern
  BaseFeature = -> Pocket013
  Direction = -> Sketch025 [H_Axis]
  Direction2 = -> Sketch025 [H_Axis]
  Length = 65
  Length2 = 100
  Mode = 0
  Mode2 = 0
  Occurrences = 11
  Occurrences2 = 1
  Offset = 6.5
  Offset2 = 100
  Originals = -> [Pocket013]
  Refine = true
  Reversed2 = false
  SpacingPattern = [0]
  SpacingPattern2 = [0]
  Spacings = [-1,-1,-1,-1,-1,-1,-1,-1,-1,-1]
  Suppressed = false
  TransformMode = 0
FEATURE [Sketcher::SketchObject] Sketch048
  ArcFitTolerance = 1e-06
  ExternalGeometry = -> [LinearPattern]
  ExternalTypes = [0,0,0,0,0,0,0]
  FullyConstrained = true
  MakeInternals = false
  MapMode = 5
  Placement = pos=(-2.83e-14,47.1996,1.133e-13) rot=(0,0.707107,0.707107;3.14159rad)
  _ExternalGeoVersion = 1
  sketch-geometry (11):
    g0: ArcOfCircle CenterX=-32.6622 CenterY=13.1501 CenterZ=0 NormalX=0 NormalY=0 NormalZ=1 AngleXU=0 Radius=1 StartAngle=5.7277 EndAngle=8.86929
    g1: ArcOfCircle CenterX=-35.1622 CenterY=9.12224 CenterZ=0 NormalX=0 NormalY=0 NormalZ=1 AngleXU=0 Radius=1 StartAngle=2.58611 EndAngle=5.7277
    g2: LineSegment StartX=-31.8126 StartY=12.6227 StartZ=0 EndX=-34.3126 EndY=8.59488 EndZ=0
    g3: LineSegment StartX=-33.5118 StartY=13.6775 StartZ=0 EndX=-36.0118 EndY=9.64959 EndZ=0
    g4: ArcOfCircle CenterX=38.8378 CenterY=2.67766 CenterZ=0 NormalX=0 NormalY=0 NormalZ=1 AngleXU=0 Radius=1 StartAngle=5.7277 EndAngle=8.86929
    g5: ArcOfCircle CenterX=36.3378 CenterY=-1.3502 CenterZ=0 NormalX=0 NormalY=0 NormalZ=1 AngleXU=0 Radius=1 StartAngle=2.58611 EndAngle=5.7277
    g6: LineSegment StartX=39.6874 StartY=2.15031 StartZ=0 EndX=37.1874 EndY=-1.87755 EndZ=0
    g7: LineSegment StartX=37.9882 StartY=3.20502 StartZ=0 EndX=35.4882 EndY=-0.822843 EndZ=0
    g8: LineSegment [constr] StartX=-28.6622 StartY=-1.3502 StartZ=0 EndX=-35.1622 EndY=-1.3502 EndZ=0
    g9: LineSegment [constr] StartX=-26.1622 StartY=13.1501 StartZ=0 EndX=-32.6622 EndY=13.1501 EndZ=0
    g10: LineSegment [constr] StartX=29.8378 StartY=-1.3502 StartZ=0 EndX=36.3378 EndY=-1.3502 EndZ=0
  constraints (26):
    c: Tangent(g0,g2) = 1.5708
    c: Tangent(g0,g3) = -1.5708
    c: Tangent(g1,g2) = 1.5708
    c: Tangent(g1,g3) = -1.5708
    c: Equal(g0,g1)
    c: Tangent(g4,g6) = 1.5708
    c: Tangent(g4,g7) = -1.5708
    c: Tangent(g5,g6) = 1.5708
    c: Tangent(g5,g7) = -1.5708
    c: Equal(g4,g5)
    c: Equal(g1,g-6)
    c: Parallel(g2,g-3)
    c: Vertical(g-6,g1)
    c: Horizontal(g-4,g0)
    c: Parallel(g-5,g7)
    c: Equal(g-7,g5)
    c: Horizontal(g-7,g5)
    c: Vertical(g-8,g4)
    c: Coincident(g8,g-7)
    c: Coincident(g8,g-6)
    c: Coincident(g9,g-4)
    c: Coincident(g9,g0)
    c: Coincident(g10,g-9)
    c: Coincident(g10,g5)
    c: Equal(g8,g9)
    c: Equal(g8,g10)
FEATURE [PartDesign::Pocket] Pocket025
  BaseFeature = -> LinearPattern
  Direction = (-1e-16,-1,-2.4e-15)
  Length = 5
  Length2 = 5
  Profile = -> Sketch048
  ReferenceAxis = -> Sketch048 [N_Axis]
  Refine = true
  SideType = 0
  Suppressed = false
  Type = 2
  Type2 = 0
FEATURE [PartDesign::Pocket] Pocket014
  BaseFeature = -> Pocket025
  Direction = (0,1,-1.8e-15)
  Length = 9.5
  Length2 = 5
  Profile = -> Sketch027
  ReferenceAxis = -> Sketch027 [N_Axis]
  Refine = true
  SideType = 0
  Suppressed = false
  Type = 0
  Type2 = 0
FEATURE [PartDesign::Pad] Pad013
  BaseFeature = -> Pocket014
  Direction = (0,0,1)
  Length = 12
  Length2 = 10
  Profile = -> Sketch031
  ReferenceAxis = -> Sketch031 [N_Axis]
  Refine = true
  SideType = 0
  Suppressed = false
  Type = 0
  Type2 = 0
FEATURE [Sketcher::SketchObject] Sketch032
  ArcFitTolerance = 1e-06
  AttachmentSupport = -> [Pad013]
  ExternalGeometry = -> [Pad013]
  ExternalTypes = [0,0]
  FullyConstrained = false
  MakeInternals = false
  MapMode = 5
  Placement = pos=(0,-25.9581,0) rot=(1,0,0;1.5708rad)
  _ExternalGeoVersion = 1
  sketch-geometry (3):
    g0: LineSegment StartX=16.7268 StartY=18.6498 StartZ=0 EndX=-31.092 EndY=30.6498 EndZ=0
    g1: LineSegment StartX=-31.092 StartY=30.6498 StartZ=0 EndX=16.7268 EndY=30.6498 EndZ=0
    g2: LineSegment StartX=16.7268 StartY=30.6498 StartZ=0 EndX=16.7268 EndY=18.6498 EndZ=0
  constraints (6):
    c: Coincident(g0,g-3)
    c: PointOnObject(g0,g-4)
    c: Coincident(g0,g1)
    c: Coincident(g1,g-4)
    c: Coincident(g1,g2)
    c: Coincident(g2,g0)
FEATURE [PartDesign::Pocket] Pocket016
  BaseFeature = -> Pad013
  Direction = (0,1,-2e-16)
  Length = 5
  Length2 = 5
  Profile = -> Sketch032
  ReferenceAxis = -> Sketch032 [N_Axis]
  Refine = true
  SideType = 0
  Suppressed = false
  Type = 2
  Type2 = 0
FEATURE [PartDesign::Pocket] Pocket018
  BaseFeature = -> Pocket016
  Direction = (-1e-16,-1,2e-16)
  Length = 54
  Length2 = 5
  Profile = -> Sketch039
  ReferenceAxis = -> Sketch039 [N_Axis]
  Refine = true
  SideType = 0
  Suppressed = false
  Type = 0
  Type2 = 0
FEATURE [PartDesign::Chamfer] Chamfer
  Angle = 45
  Base = -> Pocket018 [Vertex205,Vertex202,Edge298,Edge329,Edge297]
  BaseFeature = -> Pocket018
  ChamferType = 0
  FlipDirection = false
  Refine = true
  Size = 3.5
  Size2 = 1
  SupportTransform = false
  Suppressed = false
  UseAllEdges = false
FEATURE [PartDesign::Chamfer] Chamfer007
  Angle = 45
  Base = -> Chamfer [Edge12,Edge10,Edge99]
  BaseFeature = -> Chamfer
  ChamferType = 0
  FlipDirection = false
  Refine = true
  Size = 3.5
  Size2 = 1
  SupportTransform = false
  Suppressed = false
  UseAllEdges = false
FEATURE [PartDesign::Pocket] Pocket019
  BaseFeature = -> Chamfer007
  Direction = (0,0,1)
  Length = 14
  Length2 = 5
  Profile = -> Sketch030
  ReferenceAxis = -> Sketch030 [N_Axis]
  Refine = true
  SideType = 0
  Suppressed = false
  Type = 0
  Type2 = 0
FEATURE [PartDesign::Pad] Pad018
  BaseFeature = -> Pocket019
  Direction = (0,0,1)
  Length = 7.5
  Length2 = 10
  Profile = -> Sketch029
  ReferenceAxis = -> Sketch029 [N_Axis]
  Refine = true
  SideType = 0
  Suppressed = false
  Type = 0
  Type2 = 0
FEATURE [PartDesign::Pocket] Pocket020
  BaseFeature = -> Pad018
  Direction = (1,-2e-16,-3e-15)
  Length = 5
  Length2 = 5
  Profile = -> Sketch040
  ReferenceAxis = -> Sketch040 [N_Axis]
  Refine = true
  SideType = 0
  Suppressed = false
  Type = 2
  Type2 = 0
FEATURE [Sketcher::SketchObject] Sketch041
  ArcFitTolerance = 1e-06
  AttachmentSupport = -> [Pocket020]
  ExternalGeometry = -> [Pocket020]
  ExternalTypes = [0,0]
  FullyConstrained = true
  MakeInternals = false
  MapMode = 5
  Placement = pos=(-57.1492,3.77e-14,1.897e-13) rot=(0.57735,-0.57735,-0.57735;2.0944rad)
  _ExternalGeoVersion = 1
  sketch-geometry (12):
    g0: Circle CenterX=8.5734 CenterY=2.7 CenterZ=0 NormalX=0 NormalY=0 NormalZ=1 AngleXU=0 Radius=1.5
    g1: Circle CenterX=-15.0266 CenterY=2.7 CenterZ=0 NormalX=0 NormalY=0 NormalZ=1 AngleXU=0 Radius=1.5
    g2: Circle CenterX=-15.0266 CenterY=26.3 CenterZ=0 NormalX=0 NormalY=0 NormalZ=1 AngleXU=0 Radius=1.5
    g3: Circle CenterX=8.5734 CenterY=26.3 CenterZ=0 NormalX=0 NormalY=0 NormalZ=1 AngleXU=0 Radius=1.5
    g4: LineSegment [constr] StartX=8.5734 StartY=2.7 StartZ=0 EndX=-15.0266 EndY=2.7 EndZ=0
    g5: LineSegment [constr] StartX=8.5734 StartY=2.7 StartZ=0 EndX=8.5734 EndY=26.3 EndZ=0
    g6: LineSegment [constr] StartX=8.5734 StartY=26.3 StartZ=0 EndX=-15.0266 EndY=26.3 EndZ=0
    g7: LineSegment [constr] StartX=-15.0266 StartY=26.3 StartZ=0 EndX=-15.0266 EndY=2.7 EndZ=0
    g8: LineSegment [constr] StartX=10.6234 StartY=4.5 StartZ=0 EndX=8.5734 EndY=2.7 EndZ=0
    g9: LineSegment [constr] StartX=-17.0766 StartY=4.5 StartZ=0 EndX=-15.0266 EndY=2.7 EndZ=0
    g10: LineSegment [constr] StartX=8.5734 StartY=26.3 StartZ=0 EndX=10.6234 EndY=24.5 EndZ=0
    g11: LineSegment [constr] StartX=-15.0266 StartY=26.3 StartZ=0 EndX=-17.0766 EndY=24.5 EndZ=0
  constraints (28):
    c: Diameter(g0) = 3
    c: Diameter(g1) = 3
    c: Diameter(g2) = 3
    c: Diameter(g3) = 3
    c: Coincident(g4,g0)
    c: Coincident(g4,g1)
    c: Horizontal(g4)
    c: Coincident(g5,g0)
    c: Coincident(g5,g3)
    c: Vertical(g5)
    c: Coincident(g6,g3)
    c: Coincident(g6,g2)
    c: Horizontal(g6)
    c: Coincident(g7,g2)
    c: Coincident(g7,g1)
    c: Vertical(g7)
    c: Equal(g4,g5)
    c: DistanceY(g5,g5) = 23.6
    c: Coincident(g8,g-3)
    c: Coincident(g8,g0)
    c: Coincident(g9,g-4)
    c: Coincident(g9,g1)
    c: Equal(g9,g8)
    c: Coincident(g10,g3)
    c: Coincident(g10,g-3)
    c: Coincident(g11,g2)
    c: Coincident(g11,g-4)
    c: Equal(g8,g10)
FEATURE [PartDesign::Pad] Pad019
  BaseFeature = -> Pocket020
  Direction = (-1,1e-16,3.2e-15)
  Length = 2.75
  Length2 = 10
  Profile = -> Sketch041
  ReferenceAxis = -> Sketch041 [N_Axis]
  Refine = true
  Reversed = true
  SideType = 0
  Suppressed = false
  Type = 0
  Type2 = 0
FEATURE [Sketcher::SketchObject] Sketch042
  ArcFitTolerance = 1e-06
  AttachmentSupport = -> [Pad019]
  ExternalGeometry = -> [Pad019]
  ExternalTypes = [0,0]
  FullyConstrained = false
  MakeInternals = false
  MapMode = 5
  Placement = pos=(5.39381,4.9e-15,21.4938) rot=(0,1,0;0.24587rad)
  _ExternalGeoVersion = 1
  sketch-geometry (2):
    g0: Circle CenterX=-29.1603 CenterY=16.0781 CenterZ=0 NormalX=0 NormalY=0 NormalZ=1 AngleXU=0 Radius=3.22165
    g1: Circle CenterX=-29.1603 CenterY=-9.72188 CenterZ=0 NormalX=0 NormalY=0 NormalZ=1 AngleXU=0 Radius=3.22165
  constraints (3):
    c: Equal(g0,g1)
    c: Coincident(g1,g-4)
    c: Coincident(g0,g-3)
FEATURE [PartDesign::Pocket] Pocket021
  BaseFeature = -> Pad019
  Direction = (-0.2434,0,-0.969926)
  Length = 3
  Length2 = 5
  Profile = -> Sketch042
  ReferenceAxis = -> Sketch042 [N_Axis]
  Refine = true
  Reversed = true
  SideType = 0
  Suppressed = false
  Type = 1
  Type2 = 0
FEATURE [PartDesign::Chamfer] Chamfer008
  Angle = 45
  Base = -> Pocket021 [Edge612,Edge605,Edge581,Edge607,Edge611]
  BaseFeature = -> Pocket021
  ChamferType = 0
  FlipDirection = false
  Refine = true
  Size = 1.5
  Size2 = 1
  SupportTransform = false
  Suppressed = false
  UseAllEdges = false
FEATURE [PartDesign::Plane] DatumPlane002
  AttachmentSupport = -> [Chamfer009]
  Length = 107.999
  MapMode = 45
  Placement = pos=(-35.7786,-7.56765,28.6498) rot=(0.57735,0.57735,0.57735;2.0944rad)
  ResizeMode = 0
  Width = 134.358
FEATURE [PartDesign::Body] Body001  label="body"
  AllowCompound = false
  Group = -> [Binder001,Sketch010,Pad003,Sketch011,Pad004,Sketch013,Pocket008,Sketch014,Pocket009,Sketch015,Pad005,Pocket024,Sketch047,Sketch025,Pocket013,LinearPattern,Pocket025,Sketch048,Sketch027,Pocket014,Pad013,Pocket016,Sketch031,Sketch032,Sketch039,Pocket018,Chamfer,Chamfer007,Sketch030,Sketch029,Pocket019,DatumPlane002,Pad018,Sketch040,Pocket020,Sketch041,Pad019,Sketch042,Pocket021,Chamfer008,+7 more]
  Origin = -> Origin
  Tip = -> Pocket036
COMPONENT P3 — recipe-attached ("logo-outline", modeled in this document).
Construction recipe (the document's own serialized feature program — sketch geometry with constraints, then the solid features built on it; lengths are millimeters unless a unit is written):

FEATURE [Sketcher::SketchObject] Sketch021
  ArcFitTolerance = 1e-06
  AttachmentOffset = pos=(-61,-21,40.75) rot=(0,1,0;0rad)
  AttachmentSupport = -> [XZ_Plane]
  ExternalTypes = [0]
  FullyConstrained = false
  MakeInternals = false
  MapMode = 5
  Placement = pos=(-61,-40.75,-21) rot=(1,0,0;1.5708rad)
  _ExternalGeoVersion = 0
  sketch-geometry (10):
    g0: LineSegment StartX=16.4753 StartY=20.5288 StartZ=0 EndX=25.4753 EndY=20.5288 EndZ=0
    g1: LineSegment StartX=28.4753 StartY=23.5288 StartZ=0 EndX=28.4753 EndY=32.5288 EndZ=0
    g2: LineSegment StartX=25.4753 StartY=35.5288 StartZ=0 EndX=16.4753 EndY=35.5288 EndZ=0
    g3: LineSegment StartX=13.4753 StartY=32.5288 StartZ=0 EndX=13.4753 EndY=23.5288 EndZ=0
    g4: ArcOfCircle CenterX=16.4753 CenterY=23.5288 CenterZ=0 NormalX=0 NormalY=0 NormalZ=1 AngleXU=0 Radius=3 StartAngle=3.14159 EndAngle=4.71239
    g5: ArcOfCircle CenterX=25.4753 CenterY=23.5288 CenterZ=0 NormalX=0 NormalY=0 NormalZ=1 AngleXU=0 Radius=3 StartAngle=4.71239 EndAngle=6.28319
    g6: ArcOfCircle CenterX=25.4753 CenterY=32.5288 CenterZ=0 NormalX=0 NormalY=0 NormalZ=1 AngleXU=0 Radius=3 StartAngle=0 EndAngle=1.5708
    g7: ArcOfCircle CenterX=16.4753 CenterY=32.5288 CenterZ=0 NormalX=0 NormalY=0 NormalZ=1 AngleXU=0 Radius=3 StartAngle=1.5708 EndAngle=3.14159
    g8: GeomPoint [constr] X=13.4753 Y=20.5288 Z=0
    g9: GeomPoint [constr] X=28.4753 Y=35.5288 Z=0
  constraints (22):
    c: Tangent(g0,g4) = -1.5708
    c: Tangent(g0,g5) = -1.5708
    c: Tangent(g1,g5) = -1.5708
    c: Tangent(g1,g6) = -1.5708
    c: Tangent(g2,g6) = -1.5708
    c: Tangent(g2,g7) = -1.5708
    c: Tangent(g3,g7) = -1.5708
    c: Tangent(g3,g4) = -1.5708
    c: Horizontal(g0)
    c: Horizontal(g2)
    c: Vertical(g1)
    c: Vertical(g3)
    c: Equal(g4,g5)
    c: Equal(g5,g6)
    c: Equal(g6,g7)
    c: PointOnObject(g8,g0)
    c: PointOnObject(g8,g3)
    c: PointOnObject(g9,g1)
    c: PointOnObject(g9,g2)
    c: Distance(g1,g3) = 15
    c: Distance(g0,g2) = 15
    c: Radius(g5) = 3
FEATURE [PartDesign::Pad] Pad008
  Direction = (0,-1,2e-16)
  Length = 1
  Length2 = 10
  Placement = pos=(0,0,0) rot=(1,0,0;1.5708rad)
  Profile = -> Sketch021
  ReferenceAxis = -> Sketch021 [N_Axis]
  Refine = true
  Reversed = true
  SideType = 0
  Suppressed = false
  Type = 0
  Type2 = 0
FEATURE [PartDesign::Body] Body002  label="logo-outline"
  AllowCompound = false
  Group = -> [Sketch021,Pad008]
  Origin = -> Origin062
  Placement = pos=(0,-0.4,0) rot=(0,0,1;0rad)
  Tip = -> Pad008
COMPONENT P4 — recipe-attached ("logo-controller", modeled in this document).
Construction recipe (the document's own serialized feature program — sketch geometry with constraints, then the solid features built on it; lengths are millimeters unless a unit is written):

FEATURE [PartDesign::SubShapeBinder] Binder002
  BindCopyOnChange = 0
  BindMode = 0
  ClaimChildren = false
  Context = -> Body003 [Binder002.]
  Fuse = false
  MakeFace = true
  OffsetFill = false
  OffsetIntersection = false
  OffsetJoinType = 0
  OffsetOpenResult = false
  PartialLoad = false
  Refine = true
  Relative = true
  Support = -> [Body002,Sketch022]
  _Version = 2
FEATURE [Sketcher::SketchObject] Sketch022
  ArcFitTolerance = 1e-06
  AttachmentOffset = pos=(-8.4,-59,40.75) rot=(0,0,-1;1.5708rad)
  AttachmentSupport = -> [XZ_Plane063]
  ExternalTypes = [0]
  FullyConstrained = false
  MakeInternals = false
  MapMode = 5
  Placement = pos=(-8.4,-40.75,-59) rot=(0.57735,0.57735,-0.57735;2.0944rad)
  _ExternalGeoVersion = 0
  sketch-geometry (18):
    g0: BSplineCurve PolesCount=2 KnotsCount=2 Degree=1 IsPeriodic=0
    g1: BSplineCurve PolesCount=4 KnotsCount=2 Degree=3 IsPeriodic=0
    g2: BSplineCurve PolesCount=4 KnotsCount=2 Degree=3 IsPeriodic=0
    g3: BSplineCurve PolesCount=4 KnotsCount=2 Degree=3 IsPeriodic=0
    g4: BSplineCurve PolesCount=4 KnotsCount=2 Degree=3 IsPeriodic=0
    g5: BSplineCurve PolesCount=4 KnotsCount=2 Degree=3 IsPeriodic=0
    g6: BSplineCurve PolesCount=4 KnotsCount=2 Degree=3 IsPeriodic=0
    g7: BSplineCurve PolesCount=2 KnotsCount=2 Degree=1 IsPeriodic=0
    g8: BSplineCurve PolesCount=2 KnotsCount=2 Degree=1 IsPeriodic=0
    g9: BSplineCurve PolesCount=2 KnotsCount=2 Degree=1 IsPeriodic=0
    g10: BSplineCurve PolesCount=4 KnotsCount=2 Degree=3 IsPeriodic=0
    g11: BSplineCurve PolesCount=4 KnotsCount=2 Degree=3 IsPeriodic=0
    g12: BSplineCurve PolesCount=4 KnotsCount=2 Degree=3 IsPeriodic=0
    g13: BSplineCurve PolesCount=4 KnotsCount=2 Degree=3 IsPeriodic=0
    g14: BSplineCurve PolesCount=2 KnotsCount=2 Degree=1 IsPeriodic=0
    g15: BSplineCurve PolesCount=4 KnotsCount=2 Degree=3 IsPeriodic=0
    g16: BSplineCurve PolesCount=2 KnotsCount=2 Degree=1 IsPeriodic=0
    g17: BSplineCurve PolesCount=2 KnotsCount=2 Degree=1 IsPeriodic=0
  constraints (18):
    c: Coincident(g0,g1)
    c: Coincident(g1,g2)
    c: Coincident(g2,g3)
    c: Coincident(g3,g4)
    c: Coincident(g4,g5)
    c: Coincident(g5,g6)
    c: Coincident(g6,g7)
    c: Coincident(g7,g8)
    c: Coincident(g8,g9)
    c: Coincident(g9,g10)
    c: Coincident(g10,g11)
    c: Coincident(g11,g12)
    c: Coincident(g12,g13)
    c: Coincident(g13,g14)
    c: Coincident(g14,g15)
    c: Coincident(g15,g16)
    c: Coincident(g16,g17)
    c: Coincident(g17,g0)
FEATURE [PartDesign::Pad] Pad009
  Direction = (0,-1,2e-16)
  Length = 1
  Length2 = 10
  Placement = pos=(0,0,0) rot=(1,0,0;1.5708rad)
  Profile = -> Sketch022
  ReferenceAxis = -> Sketch022 [N_Axis]
  Refine = true
  Reversed = true
  SideType = 0
  Suppressed = false
  Type = 0
  Type2 = 0
FEATURE [PartDesign::Body] Body003  label="logo-controller"
  AllowCompound = false
  Group = -> [Binder002,Sketch022,Pad009]
  Origin = -> Origin063
  Placement = pos=(0,-0.8,0) rot=(0,0,1;0rad)
  Tip = -> Pad009
COMPONENT P5 — recipe-attached ("logo-led", modeled in this document).
Construction recipe (the document's own serialized feature program — sketch geometry with constraints, then the solid features built on it; lengths are millimeters unless a unit is written):

FEATURE [PartDesign::SubShapeBinder] Binder003
  BindCopyOnChange = 0
  BindMode = 0
  ClaimChildren = false
  Context = -> Body004 [Binder003.]
  Fuse = false
  MakeFace = true
  OffsetFill = false
  OffsetIntersection = false
  OffsetJoinType = 0
  OffsetOpenResult = false
  PartialLoad = false
  Refine = true
  Relative = true
  Support = -> [Body003,Body002]
  _Version = 2
FEATURE [Sketcher::SketchObject] Sketch023
  ArcFitTolerance = 1e-06
  AttachmentOffset = pos=(-5,0.5,40.75) rot=(0,0,1;0rad)
  AttachmentSupport = -> [XZ_Plane064]
  ExternalGeometry = -> [Binder003]
  ExternalTypes = [0]
  FullyConstrained = false
  MakeInternals = false
  MapMode = 5
  Placement = pos=(-5,-40.75,0.5) rot=(1,0,0;1.5708rad)
  _ExternalGeoVersion = 0
  sketch-geometry (4):
    g0: LineSegment StartX=-36.9059 StartY=7.32419 StartZ=0 EndX=-36.9059 EndY=11.0288 EndZ=0
    g1: ArcOfCircle CenterX=-35.0247 CenterY=11.0288 CenterZ=0 NormalX=0 NormalY=0 NormalZ=1 AngleXU=0 Radius=1.8812 StartAngle=-1.73692e-11 EndAngle=3.14159
    g2: LineSegment StartX=-33.1435 StartY=11.0288 StartZ=0 EndX=-33.1435 EndY=7.32419 EndZ=0
    g3: LineSegment StartX=-33.1435 StartY=7.32419 StartZ=0 EndX=-36.9059 EndY=7.32419 EndZ=0
  constraints (7):
    c: Tangent(g0,g1) = 1.5708
    c: Tangent(g1,g2) = 1.5708
    c: Coincident(g3,g2)
    c: Coincident(g3,g0)
    c: Symmetric(g-4,g-3,g1)
    c: Vertical(g0)
    c: Vertical(g2)
FEATURE [PartDesign::Pad] Pad010
  Direction = (0,-1,2e-16)
  Length = 1
  Length2 = 10
  Placement = pos=(0,0,0) rot=(1,0,0;1.5708rad)
  Profile = -> Sketch023
  ReferenceAxis = -> Sketch023 [N_Axis]
  Refine = true
  Reversed = true
  SideType = 0
  Suppressed = false
  Type = 0
  Type2 = 0
FEATURE [PartDesign::Body] Body004  label="logo-led"
  AllowCompound = false
  Group = -> [Binder003,Sketch023,Pad010]
  Origin = -> Origin064
  Placement = pos=(0,-0.8,0) rot=(0,0,1;0rad)
  Tip = -> Pad010
COMPONENT P6 — recipe-attached ("logo-led-outline", modeled in this document).
Construction recipe (the document's own serialized feature program — sketch geometry with constraints, then the solid features built on it; lengths are millimeters unless a unit is written):

FEATURE [PartDesign::SubShapeBinder] Binder005
  BindCopyOnChange = 0
  BindMode = 0
  ClaimChildren = false
  Context = -> Body005 [Binder005.]
  Fuse = false
  MakeFace = true
  OffsetFill = false
  OffsetIntersection = false
  OffsetJoinType = 0
  OffsetOpenResult = false
  PartialLoad = false
  Refine = true
  Relative = true
  Support = -> [Body004]
  _Version = 2
FEATURE [Sketcher::SketchObject] Sketch026
  ArcFitTolerance = 1e-06
  AttachmentOffset = pos=(-5,0.5,40.75) rot=(0,0,1;0rad)
  AttachmentSupport = -> [XZ_Plane065]
  ExternalGeometry = -> [Binder005]
  ExternalTypes = [0,0]
  FullyConstrained = false
  MakeInternals = false
  MapMode = 5
  Placement = pos=(-5,-40.75,0.5) rot=(1,0,0;1.5708rad)
  _ExternalGeoVersion = 0
  sketch-geometry (15):
    g0: LineSegment StartX=-37.5059 StartY=11.0288 StartZ=0 EndX=-37.5059 EndY=6.72419 EndZ=0
    g1: LineSegment StartX=-37.5059 StartY=6.72419 StartZ=0 EndX=-36.3747 EndY=6.72419 EndZ=0
    g2: LineSegment StartX=-32.5435 StartY=6.72419 StartZ=0 EndX=-32.5435 EndY=11.0288 EndZ=0
    g3: ArcOfCircle CenterX=-35.0247 CenterY=11.0288 CenterZ=0 NormalX=0 NormalY=0 NormalZ=1 AngleXU=0 Radius=2.4812 StartAngle=-5.9401e-12 EndAngle=3.14159
    g4: LineSegment StartX=-36.3747 StartY=6.72419 StartZ=0 EndX=-36.3747 EndY=5.8346 EndZ=0
    g5: LineSegment StartX=-36.3747 StartY=5.8346 StartZ=0 EndX=-35.7747 EndY=5.8346 EndZ=0
    g6: LineSegment StartX=-35.7747 StartY=5.8346 StartZ=0 EndX=-35.7747 EndY=6.72419 EndZ=0
    g7: LineSegment StartX=-34.2747 StartY=6.72419 StartZ=0 EndX=-34.2747 EndY=5.8346 EndZ=0
    g8: LineSegment StartX=-34.2747 StartY=5.8346 StartZ=0 EndX=-33.6747 EndY=5.8346 EndZ=0
    g9: LineSegment StartX=-33.6747 StartY=5.8346 StartZ=0 EndX=-33.6747 EndY=6.72419 EndZ=0
    g10: LineSegment [constr] StartX=-34.2747 StartY=5.8346 StartZ=0 EndX=-35.7747 EndY=5.8346 EndZ=0
    g11: LineSegment StartX=-33.6747 StartY=6.72419 StartZ=0 EndX=-32.5435 EndY=6.72419 EndZ=0
    g12: LineSegment StartX=-35.7747 StartY=6.72419 StartZ=0 EndX=-34.2747 EndY=6.72419 EndZ=0
    g13: LineSegment [constr] StartX=-36.3747 StartY=6.72419 StartZ=0 EndX=-36.9059 EndY=7.32419 EndZ=0
    g14: LineSegment [constr] StartX=-33.6747 StartY=6.72419 StartZ=0 EndX=-33.1435 EndY=7.32419 EndZ=0
  constraints (40):
    c: Coincident(g0,g1)
    c: Coincident(g11,g2)
    c: Tangent(g2,g3) = -1.5708
    c: Coincident(g3,g0)
    c: Horizontal(g0,g-3)
    c: Horizontal(g2,g-4)
    c: Symmetric(g-3,g-4,g3)
    c: Vertical(g0)
    c: Distance(g0,g-3) = 0.6
    c: Coincident(g4,g5)
    c: Coincident(g5,g6)
    c: Vertical(g4)
    c: Vertical(g6)
    c: Horizontal(g5)
    c: Distance(g4,g6) = 0.6
    c: Coincident(g7,g8)
    c: Coincident(g8,g9)
    c: Vertical(g7)
    c: Vertical(g9)
    c: Horizontal(g8)
    c: Distance(g7,g9) = 0.6
    c: Distance(g10) = 1.5
    c: Coincident(g10,g7)
    c: Coincident(g10,g5)
    c: Distance(g-4,g11) = 0.6
    c: Horizontal(g11)
    c: Coincident(g7,g12)
    c: Coincident(g11,g9)
    c: Horizontal(g1)
    c: Horizontal(g12)
    c: Coincident(g4,g1)
    c: Coincident(g12,g6)
    c: Horizontal(g10)
    c: Horizontal(g9,g7)
    c: Horizontal(g6,g1)
    c: Coincident(g13,g1)
    c: Coincident(g13,g-3)
    c: Coincident(g14,g9)
    c: Coincident(g14,g-4)
    c: Equal(g14,g13)
FEATURE [PartDesign::Pad] Pad011
  Direction = (0,-1,2e-16)
  Length = 1
  Length2 = 10
  Placement = pos=(0,0,0) rot=(1,0,0;1.5708rad)
  Profile = -> Sketch026
  ReferenceAxis = -> Sketch026 [N_Axis]
  Refine = true
  Reversed = true
  SideType = 0
  Suppressed = false
  Type = 0
  Type2 = 0
FEATURE [PartDesign::Body] Body005  label="logo-led-outline"
  AllowCompound = false
  Group = -> [Sketch026,Pad011,Binder005]
  Origin = -> Origin065
  Placement = pos=(0,-0.8,0) rot=(0,0,1;0rad)
  Tip = -> Pad011
COMPONENT P7 — recipe-attached ("logo-controller-button", modeled in this document).
Construction recipe (the document's own serialized feature program — sketch geometry with constraints, then the solid features built on it; lengths are millimeters unless a unit is written):

FEATURE [Sketcher::SketchObject] Sketch043
  ArcFitTolerance = 1e-06
  AttachmentOffset = pos=(-39.25,-6.5,40.75) rot=(0,0,1;0rad)
  AttachmentSupport = -> [Origin101]
  ExternalTypes = [0]
  FullyConstrained = false
  MakeInternals = false
  MapMode = 5
  Placement = pos=(-39.25,-40.75,-6.5) rot=(1,0,0;1.5708rad)
  _ExternalGeoVersion = 1
  sketch-geometry (1):
    g0: Circle CenterX=1.43804 CenterY=10.3162 CenterZ=0 NormalX=0 NormalY=0 NormalZ=1 AngleXU=0 Radius=0.735815
FEATURE [PartDesign::Pad] Pad020
  Direction = (0,-1,2e-16)
  Length = 1
  Length2 = 10
  Profile = -> Sketch043
  ReferenceAxis = -> Sketch043 [N_Axis]
  Refine = true
  Reversed = true
  SideType = 0
  Suppressed = false
  Type = 0
  Type2 = 0
FEATURE [PartDesign::Body] Body006  label="logo-controller-button"
  AllowCompound = false
  Group = -> [Sketch043,Pad020]
  Origin = -> Origin101
  Placement = pos=(0,-1.2,0) rot=(0,0,1;0rad)
  Tip = -> Pad020
COMPONENT P8 — recipe-attached ("logo-controller-d-pad", modeled in this document).
Construction recipe (the document's own serialized feature program — sketch geometry with constraints, then the solid features built on it; lengths are millimeters unless a unit is written):

FEATURE [Sketcher::SketchObject] Sketch044
  ArcFitTolerance = 1e-06
  AttachmentOffset = pos=(-39.25,-6.25,40.75) rot=(0,0,1;0rad)
  AttachmentSupport = -> [Origin103]
  ExternalTypes = [0]
  FullyConstrained = false
  MakeInternals = false
  MapMode = 5
  Placement = pos=(-39.25,-40.75,-6.25) rot=(1,0,0;1.5708rad)
  _ExternalGeoVersion = 1
  sketch-geometry (15):
    g0: LineSegment StartX=-3.01409 StartY=9.17394 StartZ=0 EndX=-3.01409 EndY=9.92394 EndZ=0
    g1: LineSegment StartX=-3.01409 StartY=11.1739 StartZ=0 EndX=-3.51409 EndY=11.1739 EndZ=0
    g2: LineSegment StartX=-3.51409 StartY=11.1739 StartZ=0 EndX=-3.51409 EndY=10.4239 EndZ=0
    g3: LineSegment StartX=-3.51409 StartY=9.17394 StartZ=0 EndX=-3.01409 EndY=9.17394 EndZ=0
    g4: LineSegment StartX=-2.26409 StartY=9.92394 StartZ=0 EndX=-2.26409 EndY=10.4239 EndZ=0
    g5: LineSegment StartX=-2.26409 StartY=10.4239 StartZ=0 EndX=-3.01409 EndY=10.4239 EndZ=0
    g6: LineSegment StartX=-4.26409 StartY=10.4239 StartZ=0 EndX=-4.26409 EndY=9.92394 EndZ=0
    g7: LineSegment StartX=-4.26409 StartY=9.92394 StartZ=0 EndX=-3.51409 EndY=9.92394 EndZ=0
    g8: LineSegment [constr] StartX=-3.01409 StartY=9.17394 StartZ=0 EndX=-2.26409 EndY=9.92394 EndZ=0
    g9: LineSegment [constr] StartX=-4.26409 StartY=10.4239 StartZ=0 EndX=-3.51409 EndY=11.1739 EndZ=0
    g10: LineSegment [constr] StartX=-3.01409 StartY=11.1739 StartZ=0 EndX=-2.26409 EndY=10.4239 EndZ=0
    g11: LineSegment StartX=-3.01409 StartY=9.92394 StartZ=0 EndX=-2.26409 EndY=9.92394 EndZ=0
    g12: LineSegment StartX=-3.01409 StartY=10.4239 StartZ=0 EndX=-3.01409 EndY=11.1739 EndZ=0
    g13: LineSegment StartX=-3.51409 StartY=10.4239 StartZ=0 EndX=-4.26409 EndY=10.4239 EndZ=0
    g14: LineSegment StartX=-3.51409 StartY=9.92394 StartZ=0 EndX=-3.51409 EndY=9.17394 EndZ=0
  constraints (40):
    c: Coincident(g12,g1)
    c: Coincident(g1,g2)
    c: Coincident(g14,g3)
    c: Coincident(g3,g0)
    c: Horizontal(g1)
    c: Horizontal(g3)
    c: Distance(g0,g14) = 0.5
    c: Distance(g1,g3) = 2
    c: Coincident(g4,g5)
    c: Coincident(g13,g6)
    c: Coincident(g6,g7)
    c: Coincident(g11,g4)
    c: Vertical(g4)
    c: Vertical(g6)
    c: Distance(g4,g6) = 2
    c: Distance(g5,g11) = 0.5
    c: Coincident(g8,g0)
    c: Coincident(g8,g4)
    c: Coincident(g9,g13)
    c: Coincident(g9,g1)
    c: Coincident(g10,g12)
    c: Coincident(g10,g4)
    c: Equal(g8,g10)
    c: Equal(g8,g9)
    c: Horizontal(g7)
    c: Horizontal(g11)
    c: Vertical(g0)
    c: Vertical(g12)
    c: Coincident(g11,g0)
    c: Horizontal(g5)
    c: Horizontal(g13)
    c: Coincident(g12,g5)
    c: Vertical(g2)
    c: Vertical(g14)
    c: Coincident(g7,g14)
    c: Coincident(g13,g2)
    c: Vertical(g0,g5)
    c: Vertical(g7,g2)
    c: Horizontal(g7,g0)
    c: Horizontal(g2,g5)
FEATURE [PartDesign::Pad] Pad021
  Direction = (0,-1,2e-16)
  Length = 1
  Length2 = 10
  Profile = -> Sketch044
  ReferenceAxis = -> Sketch044 [N_Axis]
  Refine = true
  Reversed = true
  SideType = 0
  Suppressed = false
  Type = 0
  Type2 = 0
FEATURE [PartDesign::Body] Body007  label="logo-controller-d-pad"
  AllowCompound = false
  Group = -> [Sketch044,Pad021]
  Origin = -> Origin103
  Placement = pos=(0,-1.2,0) rot=(0,0,1;0rad)
  Tip = -> Pad021
COMPONENT P9 — recipe-attached ("logo-outline-top", modeled in this document).
Construction recipe (the document's own serialized feature program — sketch geometry with constraints, then the solid features built on it; lengths are millimeters unless a unit is written):

FEATURE [PartDesign::FeatureBase] Clone
  BaseFeature = -> Body002
  Placement = pos=(72,34,58.4) rot=(1,0,0;1.5708rad)
  Suppressed = false
FEATURE [PartDesign::Body] Body008  label="logo-outline-top"
  AllowCompound = false
  Group = -> [Clone]
  Origin = -> Origin105
  Placement = pos=(0,0,0.25) rot=(0,0,1;0rad)
  Tip = -> Clone
COMPONENT P10 — recipe-attached ("logo-controller-top", modeled in this document).
Construction recipe (the document's own serialized feature program — sketch geometry with constraints, then the solid features built on it; lengths are millimeters unless a unit is written):

FEATURE [PartDesign::FeatureBase] Clone001
  BaseFeature = -> Body003
  Placement = pos=(24.75,58.4,-67) rot=(0,1,0;1.5708rad)
  Suppressed = false
FEATURE [PartDesign::Body] Body009  label="logo-controller-top"
  AllowCompound = false
  Group = -> [Clone001]
  Origin = -> Origin107
  Placement = pos=(0,0,0.4) rot=(1,0,0;1.5708rad)
  Tip = -> Clone001
COMPONENT P11 — recipe-attached ("logo-led-outline-top", modeled in this document).
Construction recipe (the document's own serialized feature program — sketch geometry with constraints, then the solid features built on it; lengths are millimeters unless a unit is written):

FEATURE [PartDesign::FeatureBase] Clone002
  BaseFeature = -> Body005
  Placement = pos=(24.75,58.4,-67) rot=(0,1,0;1.5708rad)
  Suppressed = false
FEATURE [PartDesign::Body] Body010  label="logo-led-outline-top"
  AllowCompound = false
  Group = -> [Clone002]
  Origin = -> Origin109
  Placement = pos=(0,0,0.4) rot=(1,0,0;1.5708rad)
  Tip = -> Clone002
COMPONENT P12 — recipe-attached ("logo-led-top", modeled in this document).
Construction recipe (the document's own serialized feature program — sketch geometry with constraints, then the solid features built on it; lengths are millimeters unless a unit is written):

FEATURE [PartDesign::FeatureBase] Clone003
  BaseFeature = -> Body004
  Placement = pos=(24.75,58.4,-67) rot=(0,1,0;1.5708rad)
  Suppressed = false
FEATURE [PartDesign::Body] Body011  label="logo-led-top"
  AllowCompound = false
  Group = -> [Clone003]
  Origin = -> Origin111
  Placement = pos=(0,0,0.4) rot=(1,0,0;1.5708rad)
  Tip = -> Clone003
COMPONENT P13 — recipe-attached ("logo-led-reflection", modeled in this document).
Construction recipe (the document's own serialized feature program — sketch geometry with constraints, then the solid features built on it; lengths are millimeters unless a unit is written):

FEATURE [Sketcher::SketchObject] Sketch049
  ArcFitTolerance = 1e-06
  AttachmentOffset = pos=(-39.25,-6.5,40.75) rot=(0,0,1;0rad)
  AttachmentSupport = -> [Origin113]
  ExternalTypes = [0]
  FullyConstrained = false
  MakeInternals = false
  MapMode = 5
  Placement = pos=(-39.25,-40.75,-6.5) rot=(1,0,0;1.5708rad)
  _ExternalGeoVersion = 1
  sketch-geometry (4):
    g0: ArcOfCircle CenterX=-1.15366 CenterY=18.7669 CenterZ=0 NormalX=0 NormalY=0 NormalZ=1 AngleXU=0 Radius=0.3 StartAngle=5.65967 EndAngle=8.80126
    g1: ArcOfCircle CenterX=-1.7526 CenterY=17.9341 CenterZ=0 NormalX=0 NormalY=0 NormalZ=1 AngleXU=0 Radius=0.3 StartAngle=2.51807 EndAngle=5.65967
    g2: LineSegment StartX=-0.910112 StartY=18.5917 StartZ=0 EndX=-1.50906 EndY=17.759 EndZ=0
    g3: LineSegment StartX=-1.39721 StartY=18.9421 StartZ=0 EndX=-1.99615 EndY=18.1093 EndZ=0
  constraints (6):
    c: Tangent(g0,g2) = 1.5708
    c: Tangent(g0,g3) = -1.5708
    c: Tangent(g1,g2) = 1.5708
    c: Tangent(g1,g3) = -1.5708
    c: Equal(g0,g1)
    c: Radius(g0) = 0.3
FEATURE [PartDesign::Pad] Pad022
  Direction = (0,-1,2e-16)
  Length = 1
  Length2 = 10
  Profile = -> Sketch049
  ReferenceAxis = -> Sketch049 [N_Axis]
  Refine = true
  Reversed = true
  SideType = 0
  Suppressed = false
  Type = 0
  Type2 = 0
FEATURE [PartDesign::Body] Body012  label="logo-led-reflection"
  AllowCompound = false
  Group = -> [Sketch049,Pad022]
  Origin = -> Origin113
  Placement = pos=(0,-0.8,0) rot=(0,0,1;0rad)
  Tip = -> Pad022
COMPONENT P14 — recipe-attached ("logo-led-reflection-top", modeled in this document).
Construction recipe (the document's own serialized feature program — sketch geometry with constraints, then the solid features built on it; lengths are millimeters unless a unit is written):

FEATURE [PartDesign::FeatureBase] Clone004
  BaseFeature = -> Body012
  Placement = pos=(77.75,58.4,-39.5) rot=(0,1,0;0rad)
  Suppressed = false
FEATURE [PartDesign::Body] Body013  label="logo-led-reflection-top"
  AllowCompound = false
  Group = -> [Clone004]
  Origin = -> Origin115
  Placement = pos=(0,0,0.4) rot=(1,0,0;1.5708rad)
  Tip = -> Clone004
COMPONENT P15 — recipe-attached ("logo-controller-button-top", modeled in this document).
Construction recipe (the document's own serialized feature program — sketch geometry with constraints, then the solid features built on it; lengths are millimeters unless a unit is written):

FEATURE [PartDesign::FeatureBase] Clone005
  BaseFeature = -> Body006
  Placement = pos=(66.25,58.4,-28.5) rot=(0,1,0;0rad)
  Suppressed = false
FEATURE [PartDesign::Body] Body014  label="logo-controller-button-top"
  AllowCompound = false
  Group = -> [Clone005]
  Origin = -> Origin117
  Placement = pos=(0,0,0.5) rot=(1,0,0;1.5708rad)
  Tip = -> Clone005
COMPONENT P16 — recipe-attached ("logo-controller-d-pad-top", modeled in this document).
Construction recipe (the document's own serialized feature program — sketch geometry with constraints, then the solid features built on it; lengths are millimeters unless a unit is written):

FEATURE [PartDesign::FeatureBase] Clone006
  BaseFeature = -> Body007
  Placement = pos=(71,58.4,-33.5) rot=(0,0,1;0rad)
  Suppressed = false
FEATURE [PartDesign::Body] Body015  label="logo-controller-d-pad-top"
  AllowCompound = false
  Group = -> [Clone006]
  Origin = -> Origin119
  Placement = pos=(0,0,0.5) rot=(1,0,0;1.5708rad)
  Tip = -> Clone006
